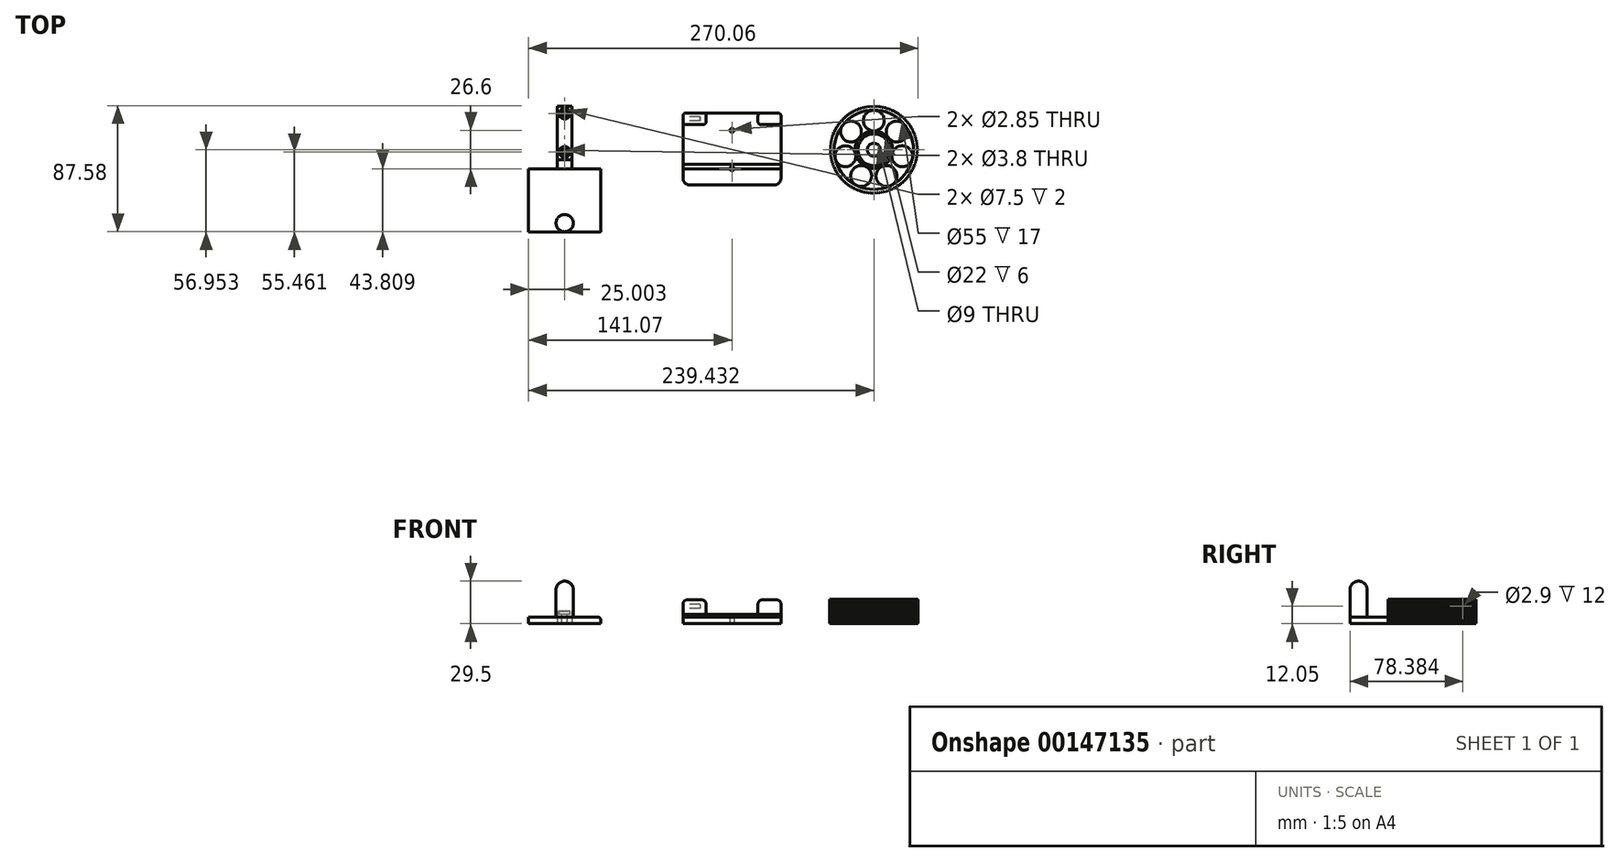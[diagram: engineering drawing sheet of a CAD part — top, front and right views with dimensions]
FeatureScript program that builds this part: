
annotation { "Feature Type Name" : "Feature", "Feature Type Description" : "" }
export const myFeature = defineFeature(function(context is Context, id is Id, definition is map)
    precondition{}
    {
        {
            var Q0;
            Q0=qCreatedBy(makeId("Top.planeOp"),FACE);
            var sketch = newSketch(context, id + "F0", { "sketchPlane" : qUnion([Q0])});
            skLineSegment(sketch, "E0.bottom", {"start": v(-34, 21.3) * mm, "end": v(34, 21.3) * mm});
            skLineSegment(sketch, "E0.top", {"start": v(-34, -28.7) * mm, "end": v(34, -28.7) * mm});
            skLineSegment(sketch, "E0.left", {"start": v(-34, 21.3) * mm, "end": v(-34, -28.7) * mm});
            skLineSegment(sketch, "E0.right", {"start": v(34, 21.3) * mm, "end": v(34, -28.7) * mm});
            skCircle(sketch, "E1", {"center": v(0, 9.32) * mm, "radius": 1.43 * mm});
            skCircle(sketch, "E2", {"center": v(0, -17.28) * mm, "radius": 1.43 * mm});
            skSolve(sketch);
        }
        {
            var Q0;
            Q0=makeQuery(id+"F0.imprint","IMPRINT",FACE,{"disambiguationData":[TD([[makeQuery(id+"F0.imprint","IMPRINT",EDGE,{"derivedFrom":sQuery(id+"F0.wireOp",EDGE,"E0.bottom")}),-1.0]])]});
            extrude(context, id + "F1", {"entities" : qUnion([Q0]), "depth" : 6.5 * mm});
        }
        {
            var Q0;
            Q0=makeQuery(id+"F1.opExtrude","CAP_FACE",FACE,{"disambiguationData":[OSD([sQuery(id+"F0.wireOp",EDGE,"E0.bottom"),sQuery(id+"F0.wireOp",EDGE,"E0.top"),sQuery(id+"F0.wireOp",EDGE,"E0.left"),sQuery(id+"F0.wireOp",EDGE,"E0.right"),sQuery(id+"F0.wireOp",EDGE,"E1"),sQuery(id+"F0.wireOp",EDGE,"E2")])],"isStart":false});
            var sketch = newSketch(context, id + "F2", { "sketchPlane" : qUnion([Q0])});
            skLineSegment(sketch, "E3.bottom", {"start": v(-34, 21.3) * mm, "end": v(-18, 21.3) * mm});
            skLineSegment(sketch, "E3.top", {"start": v(-34, 13.3) * mm, "end": v(-18, 13.3) * mm});
            skLineSegment(sketch, "E3.left", {"start": v(-34, 21.3) * mm, "end": v(-34, 13.3) * mm});
            skLineSegment(sketch, "E3.right", {"start": v(-18, 21.3) * mm, "end": v(-18, 13.3) * mm});
            skLineSegment(sketch, "E4.bottom", {"start": v(34, 21.3) * mm, "end": v(18, 21.3) * mm});
            skLineSegment(sketch, "E4.top", {"start": v(34, 13.3) * mm, "end": v(18, 13.3) * mm});
            skLineSegment(sketch, "E4.left", {"start": v(34, 21.3) * mm, "end": v(34, 13.3) * mm});
            skLineSegment(sketch, "E4.right", {"start": v(18, 21.3) * mm, "end": v(18, 13.3) * mm});
            skSolve(sketch);
        }
        {
            var Q0;
            Q0=makeQuery(id+"F2.imprint","IMPRINT",FACE,{"disambiguationData":[TD([[makeQuery(id+"F2.imprint","IMPRINT",EDGE,{"derivedFrom":sQuery(id+"F2.wireOp",EDGE,"E3.bottom")}),-1.0]])]});
            var Q1;
            Q1=makeQuery(id+"F2.imprint","IMPRINT",FACE,{"disambiguationData":[TD([[makeQuery(id+"F2.imprint","IMPRINT",EDGE,{"derivedFrom":sQuery(id+"F2.wireOp",EDGE,"E4.bottom")}),-1.0]])]});
            extrude(context, id + "F3", {"entities" : qUnion([Q0, Q1]), "operationType" : NewBodyOperationType.ADD, "depth" : 10 * mm});
        }
        {
            var Q0;
            Q0=makeQuery(id+"F3.boolean.opBoolean","MERGE",FACE,{"derivedFrom":[makeQuery(id+"F1.opExtrude","SWEPT_FACE",FACE,{"disambiguationData":[OSD([sQuery(id+"F0.wireOp",EDGE,"E0.left")])]}),makeQuery(id+"F3.opExtrude","SWEPT_FACE",FACE,{"disambiguationData":[OSD([sQuery(id+"F2.wireOp",EDGE,"E3.left")])]})]});
            var sketch = newSketch(context, id + "F4", { "sketchPlane" : qUnion([Q0])});
            skCircle(sketch, "E5", {"center": v(-17.3, 12.05) * mm, "radius": 1.45 * mm});
            skSolve(sketch);
        }
        {
            var Q0;
            Q0=makeQuery(id+"F4.imprint","IMPRINT",FACE,{"disambiguationData":[TD([[makeQuery(id+"F4.imprint","IMPRINT",EDGE,{"derivedFrom":sQuery(id+"F4.wireOp",EDGE,"E5")}),1.0]])]});
            extrude(context, id + "F5", {"entities" : qUnion([Q0]), "operationType" : NewBodyOperationType.REMOVE, "oppositeDirection" : true, "depth" : 12 * mm});
        }
        {
            var Q0;
            Q0=makeQuery(id+"F1.opExtrude","SWEPT_EDGE",EDGE,{"disambiguationData":[OSD([sQuery(id+"F0.wireOp",EDGE,"E0.top"),sQuery(id+"F0.wireOp",EDGE,"E0.left")])]});
            var Q1;
            Q1=makeQuery(id+"F1.opExtrude","SWEPT_EDGE",EDGE,{"disambiguationData":[OSD([sQuery(id+"F0.wireOp",EDGE,"E0.top"),sQuery(id+"F0.wireOp",EDGE,"E0.right")])]});
            fillet(context, id + "F6", {"entities" : qUnion([Q0, Q1]), "radius" : 5 * mm, "tangentPropagation" : true, "allowEdgeOverflow" : false});
        }
        {
            var Q0;
            Q0=makeQuery(id+"F3.opExtrude","CAP_EDGE",EDGE,{"disambiguationData":[OSD([sQuery(id+"F2.wireOp",EDGE,"E3.left")])],"isStart":false});
            var Q1;
            Q1=makeQuery(id+"F3.opExtrude","CAP_EDGE",EDGE,{"disambiguationData":[OSD([sQuery(id+"F2.wireOp",EDGE,"E4.left")])],"isStart":false});
            var Q2;
            Q2=makeQuery(id+"F3.opExtrude","CAP_EDGE",EDGE,{"disambiguationData":[OSD([sQuery(id+"F2.wireOp",EDGE,"E3.right")])],"isStart":false});
            var Q3;
            Q3=makeQuery(id+"F3.opExtrude","CAP_EDGE",EDGE,{"disambiguationData":[OSD([sQuery(id+"F2.wireOp",EDGE,"E4.right")])],"isStart":false});
            fillet(context, id + "F7", {"entities" : qUnion([Q0, Q1, Q2, Q3]), "radius" : 3 * mm, "tangentPropagation" : true, "allowEdgeOverflow" : false});
        }
        {
            var Q0;
            Q0=qCreatedBy(makeId("Top.planeOp"),FACE);
            var sketch = newSketch(context, id + "F8", { "sketchPlane" : qUnion([Q0])});
            skLineSegment(sketch, "E6.bottom", {"start": v(-121.07, 25.97) * mm, "end": v(-111.07, 25.97) * mm});
            skLineSegment(sketch, "E6.left", {"start": v(-121.07, 25.97) * mm, "end": v(-121.07, -17.53) * mm});
            skLineSegment(sketch, "E6.right", {"start": v(-111.07, 25.97) * mm, "end": v(-111.07, -17.53) * mm});
            skLineSegment(sketch, "E7.bottom", {"start": v(-141.07, -17.53) * mm, "end": v(-121.07, -17.53) * mm});
            skLineSegment(sketch, "E7.top", {"start": v(-141.07, -61.1) * mm, "end": v(-91.07, -61.1) * mm});
            skLineSegment(sketch, "E7.left", {"start": v(-141.07, -17.53) * mm, "end": v(-141.07, -61.1) * mm});
            skLineSegment(sketch, "E7.right", {"start": v(-91.07, -17.53) * mm, "end": v(-91.07, -61.1) * mm});
            skLineSegment(sketch, "E8.trimOffspring", {"start": v(-111.07, -17.53) * mm, "end": v(-91.07, -17.53) * mm});
            skSolve(sketch);
        }
        {
            var Q0;
            Q0=makeQuery(id+"F8.imprint","IMPRINT",FACE,{"disambiguationData":[TD([[makeQuery(id+"F8.imprint","IMPRINT",EDGE,{"derivedFrom":sQuery(id+"F8.wireOp",EDGE,"E6.bottom")}),-1.0]])]});
            extrude(context, id + "F9", {"entities" : qUnion([Q0]), "depth" : 8.5 * mm});
        }
        {
            var Q0;
            Q0=makeQuery(id+"F9.opExtrude","SWEPT_FACE",FACE,{"disambiguationData":[OSD([sQuery(id+"F8.wireOp",EDGE,"E7.left")])]});
            var sketch = newSketch(context, id + "F10", { "sketchPlane" : qUnion([Q0])});
            skLineSegment(sketch, "E9", {"start": v(61.1, 4.5) * mm, "end": v(17.53, 4.5) * mm});
            skLineSegment(sketch, "E10", {"start": v(17.53, 4.5) * mm, "end": v(11.03, 8.5) * mm});
            skLineSegment(sketch, "E11", {"start": v(11.03, 8.5) * mm, "end": v(61.1, 8.5) * mm});
            skLineSegment(sketch, "E12", {"start": v(61.1, 8.5) * mm, "end": v(61.1, 4.5) * mm});
            skSolve(sketch);
        }
        {
            var Q0;
            {var subQ0=sQuery(id+"F10.wireOp",EDGE,"E10");Q0=makeQuery(id+"F10.imprint","IMPRINT",FACE,{"disambiguationData":[TD([[makeQuery(id+"F10.imprint","IMPRINT",EDGE,{"derivedFrom":subQ0}),-1.0]])]});}
            var Q1;
            {var subQ0=sQuery(id+"F10.wireOp",EDGE,"E9");Q1=makeQuery(id+"F10.imprint","IMPRINT",FACE,{"disambiguationData":[TD([[makeQuery(id+"F10.imprint","IMPRINT",EDGE,{"derivedFrom":subQ0}),-1.0]])]});}
            extrude(context, id + "F11", {"entities" : qUnion([Q0, Q1]), "operationType" : NewBodyOperationType.REMOVE, "endBound" : BoundingType.THROUGH_ALL, "oppositeDirection" : true, "depth" : 25 * mm});
        }
        {
            var Q0;
            Q0=makeQuery(id+"F9.opExtrude","CAP_FACE",FACE,{"disambiguationData":[OSD([sQuery(id+"F8.wireOp",EDGE,"E6.bottom"),sQuery(id+"F8.wireOp",EDGE,"E6.left"),sQuery(id+"F8.wireOp",EDGE,"E6.right"),sQuery(id+"F8.wireOp",EDGE,"E7.bottom"),sQuery(id+"F8.wireOp",EDGE,"E7.top"),sQuery(id+"F8.wireOp",EDGE,"E7.left"),sQuery(id+"F8.wireOp",EDGE,"E7.right"),sQuery(id+"F8.wireOp",EDGE,"E8.trimOffspring")])],"isStart":false});
            var sketch = newSketch(context, id + "F12", { "sketchPlane" : qUnion([Q0])});
            skLineSegment(sketch, "E13", {"start": v(-116.07, 25.97) * mm, "end": v(-116.07, -11.03) * mm, "construction": true});
            skCircle(sketch, "E14", {"center": v(-116.07, 20.97) * mm, "radius": 3.75 * mm});
            skCircle(sketch, "E15", {"center": v(-116.07, -5.63) * mm, "radius": 3.75 * mm});
            skCircle(sketch, "E16", {"center": v(-116.07, 20.97) * mm, "radius": 1.9 * mm});
            skCircle(sketch, "E17", {"center": v(-116.07, -5.63) * mm, "radius": 1.9 * mm});
            skSolve(sketch);
        }
        {
            var Q0;
            Q0=makeQuery(id+"F12.imprint","IMPRINT",FACE,{"disambiguationData":[TD([[makeQuery(id+"F12.imprint","IMPRINT",EDGE,{"derivedFrom":sQuery(id+"F12.wireOp",EDGE,"E16")}),1.0]])]});
            var Q1;
            Q1=makeQuery(id+"F12.imprint","IMPRINT",FACE,{"disambiguationData":[TD([[makeQuery(id+"F12.imprint","IMPRINT",EDGE,{"derivedFrom":sQuery(id+"F12.wireOp",EDGE,"E17")}),1.0]])]});
            extrude(context, id + "F13", {"entities" : qUnion([Q0, Q1]), "operationType" : NewBodyOperationType.REMOVE, "endBound" : BoundingType.THROUGH_ALL, "oppositeDirection" : true, "depth" : 25 * mm});
        }
        {
            var Q0;
            Q0=makeQuery(id+"F12.imprint","IMPRINT",FACE,{"disambiguationData":[TD([[makeQuery(id+"F12.imprint","IMPRINT",EDGE,{"derivedFrom":sQuery(id+"F12.wireOp",EDGE,"E14")}),1.0]])]});
            var Q1;
            Q1=makeQuery(id+"F12.imprint","IMPRINT",FACE,{"disambiguationData":[TD([[makeQuery(id+"F12.imprint","IMPRINT",EDGE,{"derivedFrom":sQuery(id+"F12.wireOp",EDGE,"E15")}),1.0]])]});
            extrude(context, id + "F14", {"entities" : qUnion([Q0, Q1]), "operationType" : NewBodyOperationType.REMOVE, "oppositeDirection" : true, "depth" : 2 * mm});
        }
        {
            var Q0;
            Q0=makeQuery(id+"F11.boolean.opBoolean","COPY",FACE,{"derivedFrom":makeQuery(id+"F11.opExtrude","SWEPT_FACE",FACE,{"disambiguationData":[OSD([sQuery(id+"F10.wireOp",EDGE,"E9")])]})});
            var sketch = newSketch(context, id + "F15", { "sketchPlane" : qUnion([Q0])});
            skCircle(sketch, "E18", {"center": v(-116.07, -55.1) * mm, "radius": 6 * mm});
            skSolve(sketch);
        }
        {
            var Q0;
            Q0=makeQuery(id+"F15.imprint","IMPRINT",FACE,{"disambiguationData":[TD([[makeQuery(id+"F15.imprint","IMPRINT",EDGE,{"derivedFrom":sQuery(id+"F15.wireOp",EDGE,"E18")}),1.0]])]});
            extrude(context, id + "F16", {"entities" : qUnion([Q0]), "operationType" : NewBodyOperationType.ADD, "depth" : 25 * mm});
        }
        {
            var Q0;
            Q0=makeQuery(id+"F16.opExtrude","CAP_EDGE",EDGE,{"disambiguationData":[OSD([sQuery(id+"F15.wireOp",EDGE,"E18")])],"isStart":false});
            fillet(context, id + "F17", {"entities" : qUnion([Q0]), "radius" : 6 * mm, "tangentPropagation" : true, "allowEdgeOverflow" : false});
        }
        {
            var Q0;
            Q0=makeQuery(id+"F11.boolean.opBoolean","COPY",EDGE,{"derivedFrom":makeQuery(id+"F11.opExtrude","CAP_EDGE",EDGE,{"disambiguationData":[OSD([sQuery(id+"F10.wireOp",EDGE,"E9")])],"isStart":true})});
            var Q1;
            {var subQ0=sQuery(id+"F8.wireOp",EDGE,"E7.top");var subQ1=sQuery(id+"F8.wireOp",EDGE,"E7.left");var subQ2=sQuery(id+"F10.wireOp",EDGE,"E9");Q1=makeQuery(id+"F16.boolean.opBoolean","SPLIT",EDGE,{"disambiguationData":[TD([makeQuery(id+"F9.opExtrude","SWEPT_FACE",FACE,{"disambiguationData":[OSD([subQ1])]})])],"derivedFrom":makeQuery(id+"F11.boolean.opBoolean","COPY",EDGE,{"derivedFrom":makeQuery(id+"F11.opExtrude","SWEPT_EDGE",EDGE,{"disambiguationData":[OSD([subQ0,subQ1,subQ2,sQuery(id+"F10.wireOp",EDGE,"E12")])]})})});}
            var Q2;
            {var subQ0=sQuery(id+"F8.wireOp",EDGE,"E7.top");var subQ1=sQuery(id+"F10.wireOp",EDGE,"E9");Q2=makeQuery(id+"F16.boolean.opBoolean","SPLIT",EDGE,{"disambiguationData":[TD([makeQuery(id+"F9.opExtrude","SWEPT_FACE",FACE,{"disambiguationData":[OSD([sQuery(id+"F8.wireOp",EDGE,"E7.right")])]})])],"derivedFrom":makeQuery(id+"F11.boolean.opBoolean","COPY",EDGE,{"derivedFrom":makeQuery(id+"F11.opExtrude","SWEPT_EDGE",EDGE,{"disambiguationData":[OSD([subQ0,sQuery(id+"F8.wireOp",EDGE,"E7.left"),subQ1,sQuery(id+"F10.wireOp",EDGE,"E12")])]})})});}
            var Q3;
            Q3=makeQuery(id+"F11.boolean.opBoolean","INTERSECT",EDGE,{"derivedFrom":[makeQuery(id+"F9.opExtrude","SWEPT_FACE",FACE,{"disambiguationData":[OSD([sQuery(id+"F8.wireOp",EDGE,"E7.right")])]}),makeQuery(id+"F11.opExtrude","SWEPT_FACE",FACE,{"disambiguationData":[OSD([sQuery(id+"F10.wireOp",EDGE,"E9")])]})]});
            fillet(context, id + "F18", {"entities" : qUnion([Q0, Q1, Q2, Q3]), "radius" : 2 * mm, "tangentPropagation" : true, "allowEdgeOverflow" : false});
        }
        {
            var Q0;
            Q0=qCreatedBy(makeId("Top.planeOp"),FACE);
            var sketch = newSketch(context, id + "F19", { "sketchPlane" : qUnion([Q0])});
            skArc(sketch, "E19", {"start": v(98.36, 25.86) * mm, "mid": v(98.14, 25.86) * mm, "end": v(97.92, 25.86) * mm});
            skCircle(sketch, "E20", {"center": v(98.36, -4.14) * mm, "radius": 27.5 * mm});
            skCircle(sketch, "E21", {"center": v(98.36, -4.14) * mm, "radius": 11 * mm});
            skCircle(sketch, "E22", {"center": v(98.36, -4.14) * mm, "radius": 13 * mm});
            skCircle(sketch, "E23", {"center": v(98.36, -4.14) * mm, "radius": 4.5 * mm});
            skLineSegment(sketch, "E24", {"start": v(98.36, -4.14) * mm, "end": v(98.36, 23.36) * mm, "construction": true});
            skCircle(sketch, "E25", {"center": v(98.36, 16.11) * mm, "radius": 7.25 * mm});
            skCircle(sketch, "E26.1.0", {"center": v(82.53, 8.49) * mm, "radius": 7.25 * mm});
            skLineSegment(sketch, "E26.1.1", {"start": v(98.36, -4.14) * mm, "end": v(76.86, 13) * mm, "construction": true});
            skCircle(sketch, "E26.2.0", {"center": v(78.62, -8.64) * mm, "radius": 7.25 * mm});
            skLineSegment(sketch, "E26.2.1", {"start": v(98.36, -4.14) * mm, "end": v(71.55, -10.26) * mm, "construction": true});
            skCircle(sketch, "E26.3.0", {"center": v(89.58, -22.38) * mm, "radius": 7.25 * mm});
            skLineSegment(sketch, "E26.3.1", {"start": v(98.36, -4.14) * mm, "end": v(86.43, -28.91) * mm, "construction": true});
            skCircle(sketch, "E26.4.0", {"center": v(107.15, -22.38) * mm, "radius": 7.25 * mm});
            skLineSegment(sketch, "E26.4.1", {"start": v(98.36, -4.14) * mm, "end": v(110.3, -28.91) * mm, "construction": true});
            skCircle(sketch, "E26.5.0", {"center": v(118.1, -8.64) * mm, "radius": 7.25 * mm});
            skLineSegment(sketch, "E26.5.1", {"start": v(98.36, -4.14) * mm, "end": v(125.17, -10.26) * mm, "construction": true});
            skLineSegment(sketch, "E27", {"start": v(98.36, 23.36) * mm, "end": v(98.36, 25.86) * mm, "construction": true});
            skLineSegment(sketch, "E28", {"start": v(98.36, 25.86) * mm, "end": v(98.82, 26.5) * mm});
            skLineSegment(sketch, "E29", {"start": v(98.82, 26.5) * mm, "end": v(99.17, 25.85) * mm});
            skLineSegment(sketch, "E30.1.0", {"start": v(97.1, 25.84) * mm, "end": v(97.53, 26.48) * mm});
            skLineSegment(sketch, "E30.1.1", {"start": v(97.53, 26.48) * mm, "end": v(97.92, 25.86) * mm});
            skLineSegment(sketch, "E30.2.0", {"start": v(95.85, 25.76) * mm, "end": v(96.25, 26.42) * mm});
            skLineSegment(sketch, "E30.2.1", {"start": v(96.25, 26.42) * mm, "end": v(96.66, 25.81) * mm});
            skLineSegment(sketch, "E30.3.0", {"start": v(94.6, 25.63) * mm, "end": v(94.97, 26.3) * mm});
            skLineSegment(sketch, "E30.3.1", {"start": v(94.97, 26.3) * mm, "end": v(95.4, 25.72) * mm});
            skLineSegment(sketch, "E30.4.0", {"start": v(93.36, 25.44) * mm, "end": v(93.7, 26.14) * mm});
            skLineSegment(sketch, "E30.4.1", {"start": v(93.7, 26.14) * mm, "end": v(94.16, 25.57) * mm});
            skLineSegment(sketch, "E30.5.0", {"start": v(92.12, 25.2) * mm, "end": v(92.44, 25.92) * mm});
            skLineSegment(sketch, "E30.5.1", {"start": v(92.44, 25.92) * mm, "end": v(92.92, 25.36) * mm});
            skLineSegment(sketch, "E30.6.0", {"start": v(90.9, 24.92) * mm, "end": v(91.19, 25.64) * mm});
            skLineSegment(sketch, "E30.6.1", {"start": v(91.19, 25.64) * mm, "end": v(91.69, 25.11) * mm});
            skLineSegment(sketch, "E30.7.0", {"start": v(89.7, 24.58) * mm, "end": v(89.95, 25.32) * mm});
            skLineSegment(sketch, "E30.7.1", {"start": v(89.95, 25.32) * mm, "end": v(90.47, 24.8) * mm});
            skLineSegment(sketch, "E30.8.0", {"start": v(88.5, 24.2) * mm, "end": v(88.72, 24.94) * mm});
            skLineSegment(sketch, "E30.8.1", {"start": v(88.72, 24.94) * mm, "end": v(89.27, 24.45) * mm});
            skLineSegment(sketch, "E30.9.0", {"start": v(87.32, 23.76) * mm, "end": v(87.5, 24.5) * mm});
            skLineSegment(sketch, "E30.9.1", {"start": v(87.5, 24.5) * mm, "end": v(88.08, 24.04) * mm});
            skLineSegment(sketch, "E30.10.0", {"start": v(86.16, 23.27) * mm, "end": v(86.32, 24.03) * mm});
            skLineSegment(sketch, "E30.10.1", {"start": v(86.32, 24.03) * mm, "end": v(86.9, 23.59) * mm});
            skLineSegment(sketch, "E30.11.0", {"start": v(85.02, 22.73) * mm, "end": v(85.15, 23.5) * mm});
            skLineSegment(sketch, "E30.11.1", {"start": v(85.15, 23.5) * mm, "end": v(85.75, 23.08) * mm});
            skLineSegment(sketch, "E30.12.0", {"start": v(83.9, 22.15) * mm, "end": v(84, 22.92) * mm});
            skLineSegment(sketch, "E30.12.1", {"start": v(84, 22.92) * mm, "end": v(84.63, 22.53) * mm});
            skLineSegment(sketch, "E30.13.0", {"start": v(82.82, 21.52) * mm, "end": v(82.88, 22.3) * mm});
            skLineSegment(sketch, "E30.13.1", {"start": v(82.88, 22.3) * mm, "end": v(83.52, 21.93) * mm});
            skLineSegment(sketch, "E30.14.0", {"start": v(81.76, 20.85) * mm, "end": v(81.8, 21.63) * mm});
            skLineSegment(sketch, "E30.14.1", {"start": v(81.8, 21.63) * mm, "end": v(82.44, 21.29) * mm});
            skLineSegment(sketch, "E30.15.0", {"start": v(80.73, 20.13) * mm, "end": v(80.73, 20.9) * mm});
            skLineSegment(sketch, "E30.15.1", {"start": v(80.73, 20.9) * mm, "end": v(81.4, 20.6) * mm});
            skLineSegment(sketch, "E30.16.0", {"start": v(79.73, 19.37) * mm, "end": v(79.7, 20.15) * mm});
            skLineSegment(sketch, "E30.16.1", {"start": v(79.7, 20.15) * mm, "end": v(80.37, 19.87) * mm});
            skLineSegment(sketch, "E30.17.0", {"start": v(78.76, 18.57) * mm, "end": v(78.7, 19.35) * mm});
            skLineSegment(sketch, "E30.17.1", {"start": v(78.7, 19.35) * mm, "end": v(79.38, 19.1) * mm});
            skLineSegment(sketch, "E30.18.0", {"start": v(77.83, 17.73) * mm, "end": v(77.73, 18.5) * mm});
            skLineSegment(sketch, "E30.18.1", {"start": v(77.73, 18.5) * mm, "end": v(78.42, 18.28) * mm});
            skLineSegment(sketch, "E30.19.0", {"start": v(76.93, 16.85) * mm, "end": v(76.8, 17.62) * mm});
            skLineSegment(sketch, "E30.19.1", {"start": v(76.8, 17.62) * mm, "end": v(77.5, 17.42) * mm});
            skLineSegment(sketch, "E30.20.0", {"start": v(76.07, 15.94) * mm, "end": v(75.9, 16.7) * mm});
            skLineSegment(sketch, "E30.20.1", {"start": v(75.9, 16.7) * mm, "end": v(76.62, 16.53) * mm});
            skLineSegment(sketch, "E30.21.0", {"start": v(75.25, 14.99) * mm, "end": v(75.05, 15.74) * mm});
            skLineSegment(sketch, "E30.21.1", {"start": v(75.05, 15.74) * mm, "end": v(75.77, 15.6) * mm});
            skLineSegment(sketch, "E30.22.0", {"start": v(74.47, 14) * mm, "end": v(74.24, 14.74) * mm});
            skLineSegment(sketch, "E30.22.1", {"start": v(74.24, 14.74) * mm, "end": v(74.97, 14.64) * mm});
            skLineSegment(sketch, "E30.23.0", {"start": v(73.73, 12.98) * mm, "end": v(73.47, 13.72) * mm});
            skLineSegment(sketch, "E30.23.1", {"start": v(73.47, 13.72) * mm, "end": v(74.2, 13.64) * mm});
            skLineSegment(sketch, "E30.24.0", {"start": v(73.03, 11.94) * mm, "end": v(72.75, 12.66) * mm});
            skLineSegment(sketch, "E30.24.1", {"start": v(72.75, 12.66) * mm, "end": v(73.48, 12.62) * mm});
            skLineSegment(sketch, "E30.25.0", {"start": v(72.38, 10.86) * mm, "end": v(72.06, 11.57) * mm});
            skLineSegment(sketch, "E30.25.1", {"start": v(72.06, 11.57) * mm, "end": v(72.8, 11.56) * mm});
            skLineSegment(sketch, "E30.26.0", {"start": v(71.78, 9.76) * mm, "end": v(71.43, 10.46) * mm});
            skLineSegment(sketch, "E30.26.1", {"start": v(71.43, 10.46) * mm, "end": v(72.16, 10.47) * mm});
            skLineSegment(sketch, "E30.27.0", {"start": v(71.22, 8.64) * mm, "end": v(70.84, 9.32) * mm});
            skLineSegment(sketch, "E30.27.1", {"start": v(70.84, 9.32) * mm, "end": v(71.57, 9.36) * mm});
            skLineSegment(sketch, "E30.28.0", {"start": v(70.7, 7.49) * mm, "end": v(70.3, 8.15) * mm});
            skLineSegment(sketch, "E30.28.1", {"start": v(70.3, 8.15) * mm, "end": v(71.03, 8.23) * mm});
            skLineSegment(sketch, "E30.29.0", {"start": v(70.24, 6.32) * mm, "end": v(69.81, 6.97) * mm});
            skLineSegment(sketch, "E30.29.1", {"start": v(69.81, 6.97) * mm, "end": v(70.54, 7.08) * mm});
            skLineSegment(sketch, "E30.30.0", {"start": v(69.83, 5.13) * mm, "end": v(69.37, 5.76) * mm});
            skLineSegment(sketch, "E30.30.1", {"start": v(69.37, 5.76) * mm, "end": v(70.1, 5.9) * mm});
            skLineSegment(sketch, "E30.31.0", {"start": v(69.47, 3.93) * mm, "end": v(68.98, 4.54) * mm});
            skLineSegment(sketch, "E30.31.1", {"start": v(68.98, 4.54) * mm, "end": v(69.7, 4.7) * mm});
            skLineSegment(sketch, "E30.32.0", {"start": v(69.15, 2.71) * mm, "end": v(68.65, 3.3) * mm});
            skLineSegment(sketch, "E30.32.1", {"start": v(68.65, 3.3) * mm, "end": v(69.35, 3.5) * mm});
            skLineSegment(sketch, "E30.33.0", {"start": v(68.9, 1.48) * mm, "end": v(68.36, 2.05) * mm});
            skLineSegment(sketch, "E30.33.1", {"start": v(68.36, 2.05) * mm, "end": v(69.06, 2.28) * mm});
            skLineSegment(sketch, "E30.34.0", {"start": v(68.68, 0.25) * mm, "end": v(68.13, 0.79) * mm});
            skLineSegment(sketch, "E30.34.1", {"start": v(68.13, 0.79) * mm, "end": v(68.81, 1.05) * mm});
            skLineSegment(sketch, "E30.35.0", {"start": v(68.53, -1) * mm, "end": v(67.95, -0.48) * mm});
            skLineSegment(sketch, "E30.35.1", {"start": v(67.95, -0.48) * mm, "end": v(68.62, -0.2) * mm});
            skLineSegment(sketch, "E30.36.0", {"start": v(68.42, -2.25) * mm, "end": v(67.82, -1.76) * mm});
            skLineSegment(sketch, "E30.36.1", {"start": v(67.82, -1.76) * mm, "end": v(68.48, -1.45) * mm});
            skLineSegment(sketch, "E30.37.0", {"start": v(68.37, -3.5) * mm, "end": v(67.75, -3.04) * mm});
            skLineSegment(sketch, "E30.37.1", {"start": v(67.75, -3.04) * mm, "end": v(68.4, -2.7) * mm});
            skLineSegment(sketch, "E30.38.0", {"start": v(68.37, -4.77) * mm, "end": v(67.73, -4.32) * mm});
            skLineSegment(sketch, "E30.38.1", {"start": v(67.73, -4.32) * mm, "end": v(68.36, -3.96) * mm});
            skLineSegment(sketch, "E30.39.0", {"start": v(68.42, -6.02) * mm, "end": v(67.77, -5.6) * mm});
            skLineSegment(sketch, "E30.39.1", {"start": v(67.77, -5.6) * mm, "end": v(68.38, -5.21) * mm});
            skLineSegment(sketch, "E30.40.0", {"start": v(68.53, -7.27) * mm, "end": v(67.85, -6.89) * mm});
            skLineSegment(sketch, "E30.40.1", {"start": v(67.85, -6.89) * mm, "end": v(68.45, -6.47) * mm});
            skLineSegment(sketch, "E30.41.0", {"start": v(68.68, -8.52) * mm, "end": v(68, -8.16) * mm});
            skLineSegment(sketch, "E30.41.1", {"start": v(68, -8.16) * mm, "end": v(68.58, -7.72) * mm});
            skLineSegment(sketch, "E30.42.0", {"start": v(68.9, -9.76) * mm, "end": v(68.2, -9.43) * mm});
            skLineSegment(sketch, "E30.42.1", {"start": v(68.2, -9.43) * mm, "end": v(68.75, -8.96) * mm});
            skLineSegment(sketch, "E30.43.0", {"start": v(69.15, -10.99) * mm, "end": v(68.44, -10.69) * mm});
            skLineSegment(sketch, "E30.43.1", {"start": v(68.44, -10.69) * mm, "end": v(68.98, -10.2) * mm});
            skLineSegment(sketch, "E30.44.0", {"start": v(69.47, -12.2) * mm, "end": v(68.74, -11.94) * mm});
            skLineSegment(sketch, "E30.44.1", {"start": v(68.74, -11.94) * mm, "end": v(69.26, -11.42) * mm});
            skLineSegment(sketch, "E30.45.0", {"start": v(69.83, -13.4) * mm, "end": v(69.1, -13.17) * mm});
            skLineSegment(sketch, "E30.45.1", {"start": v(69.1, -13.17) * mm, "end": v(69.6, -12.63) * mm});
            skLineSegment(sketch, "E30.46.0", {"start": v(70.24, -14.6) * mm, "end": v(69.5, -14.39) * mm});
            skLineSegment(sketch, "E30.46.1", {"start": v(69.5, -14.39) * mm, "end": v(69.97, -13.83) * mm});
            skLineSegment(sketch, "E30.47.0", {"start": v(70.7, -15.76) * mm, "end": v(69.95, -15.59) * mm});
            skLineSegment(sketch, "E30.47.1", {"start": v(69.95, -15.59) * mm, "end": v(70.4, -15.01) * mm});
            skLineSegment(sketch, "E30.48.0", {"start": v(71.22, -16.91) * mm, "end": v(70.45, -16.77) * mm});
            skLineSegment(sketch, "E30.48.1", {"start": v(70.45, -16.77) * mm, "end": v(70.88, -16.17) * mm});
            skLineSegment(sketch, "E30.49.0", {"start": v(71.78, -18.04) * mm, "end": v(71, -17.92) * mm});
            skLineSegment(sketch, "E30.49.1", {"start": v(71, -17.92) * mm, "end": v(71.41, -17.31) * mm});
            skLineSegment(sketch, "E30.50.0", {"start": v(72.38, -19.14) * mm, "end": v(71.6, -19.06) * mm});
            skLineSegment(sketch, "E30.50.1", {"start": v(71.6, -19.06) * mm, "end": v(71.99, -18.43) * mm});
            skLineSegment(sketch, "E30.51.0", {"start": v(73.03, -20.21) * mm, "end": v(72.26, -20.17) * mm});
            skLineSegment(sketch, "E30.51.1", {"start": v(72.26, -20.17) * mm, "end": v(72.6, -19.52) * mm});
            skLineSegment(sketch, "E30.52.0", {"start": v(73.73, -21.26) * mm, "end": v(72.95, -21.24) * mm});
            skLineSegment(sketch, "E30.52.1", {"start": v(72.95, -21.24) * mm, "end": v(73.27, -20.59) * mm});
            skLineSegment(sketch, "E30.53.0", {"start": v(74.47, -22.28) * mm, "end": v(73.7, -22.3) * mm});
            skLineSegment(sketch, "E30.53.1", {"start": v(73.7, -22.3) * mm, "end": v(73.99, -21.62) * mm});
            skLineSegment(sketch, "E30.54.0", {"start": v(75.25, -23.26) * mm, "end": v(74.47, -23.31) * mm});
            skLineSegment(sketch, "E30.54.1", {"start": v(74.47, -23.31) * mm, "end": v(74.74, -22.63) * mm});
            skLineSegment(sketch, "E30.55.0", {"start": v(76.07, -24.21) * mm, "end": v(75.3, -24.3) * mm});
            skLineSegment(sketch, "E30.55.1", {"start": v(75.3, -24.3) * mm, "end": v(75.53, -23.6) * mm});
            skLineSegment(sketch, "E30.56.0", {"start": v(76.93, -25.13) * mm, "end": v(76.16, -25.24) * mm});
            skLineSegment(sketch, "E30.56.1", {"start": v(76.16, -25.24) * mm, "end": v(76.37, -24.54) * mm});
            skLineSegment(sketch, "E30.57.0", {"start": v(77.83, -26) * mm, "end": v(77.06, -26.15) * mm});
            skLineSegment(sketch, "E30.57.1", {"start": v(77.06, -26.15) * mm, "end": v(77.24, -25.44) * mm});
            skLineSegment(sketch, "E30.58.0", {"start": v(78.76, -26.85) * mm, "end": v(78, -27.03) * mm});
            skLineSegment(sketch, "E30.58.1", {"start": v(78, -27.03) * mm, "end": v(78.15, -26.3) * mm});
            skLineSegment(sketch, "E30.59.0", {"start": v(79.73, -27.65) * mm, "end": v(78.98, -27.86) * mm});
            skLineSegment(sketch, "E30.59.1", {"start": v(78.98, -27.86) * mm, "end": v(79.1, -27.14) * mm});
            skLineSegment(sketch, "E30.60.0", {"start": v(80.73, -28.4) * mm, "end": v(80, -28.65) * mm});
            skLineSegment(sketch, "E30.60.1", {"start": v(80, -28.65) * mm, "end": v(80.08, -27.92) * mm});
            skLineSegment(sketch, "E30.61.0", {"start": v(81.76, -29.12) * mm, "end": v(81.03, -29.4) * mm});
            skLineSegment(sketch, "E30.61.1", {"start": v(81.03, -29.4) * mm, "end": v(81.1, -28.67) * mm});
            skLineSegment(sketch, "E30.62.0", {"start": v(82.82, -29.8) * mm, "end": v(82.1, -30.1) * mm});
            skLineSegment(sketch, "E30.62.1", {"start": v(82.1, -30.1) * mm, "end": v(82.13, -29.37) * mm});
            skLineSegment(sketch, "E30.63.0", {"start": v(83.9, -30.43) * mm, "end": v(83.2, -30.76) * mm});
            skLineSegment(sketch, "E30.63.1", {"start": v(83.2, -30.76) * mm, "end": v(83.2, -30.03) * mm});
            skLineSegment(sketch, "E30.64.0", {"start": v(85.02, -31) * mm, "end": v(84.34, -31.37) * mm});
            skLineSegment(sketch, "E30.64.1", {"start": v(84.34, -31.37) * mm, "end": v(84.3, -30.64) * mm});
            skLineSegment(sketch, "E30.65.0", {"start": v(86.16, -31.54) * mm, "end": v(85.49, -31.93) * mm});
            skLineSegment(sketch, "E30.65.1", {"start": v(85.49, -31.93) * mm, "end": v(85.42, -31.2) * mm});
            skLineSegment(sketch, "E30.66.0", {"start": v(87.32, -32.03) * mm, "end": v(86.66, -32.45) * mm});
            skLineSegment(sketch, "E30.66.1", {"start": v(86.66, -32.45) * mm, "end": v(86.57, -31.72) * mm});
            skLineSegment(sketch, "E30.67.0", {"start": v(88.5, -32.47) * mm, "end": v(87.86, -32.91) * mm});
            skLineSegment(sketch, "E30.67.1", {"start": v(87.86, -32.91) * mm, "end": v(87.73, -32.2) * mm});
            skLineSegment(sketch, "E30.68.0", {"start": v(89.7, -32.86) * mm, "end": v(89.07, -33.33) * mm});
            skLineSegment(sketch, "E30.68.1", {"start": v(89.07, -33.33) * mm, "end": v(88.92, -32.61) * mm});
            skLineSegment(sketch, "E30.69.0", {"start": v(90.9, -33.2) * mm, "end": v(90.3, -33.7) * mm});
            skLineSegment(sketch, "E30.69.1", {"start": v(90.3, -33.7) * mm, "end": v(90.12, -32.98) * mm});
            skLineSegment(sketch, "E30.70.0", {"start": v(92.12, -33.48) * mm, "end": v(91.55, -34) * mm});
            skLineSegment(sketch, "E30.70.1", {"start": v(91.55, -34) * mm, "end": v(91.33, -33.3) * mm});
            skLineSegment(sketch, "E30.71.0", {"start": v(93.36, -33.72) * mm, "end": v(92.8, -34.26) * mm});
            skLineSegment(sketch, "E30.71.1", {"start": v(92.8, -34.26) * mm, "end": v(92.56, -33.57) * mm});
            skLineSegment(sketch, "E30.72.0", {"start": v(94.6, -33.9) * mm, "end": v(94.07, -34.47) * mm});
            skLineSegment(sketch, "E30.72.1", {"start": v(94.07, -34.47) * mm, "end": v(93.8, -33.79) * mm});
            skLineSegment(sketch, "E30.73.0", {"start": v(95.85, -34.03) * mm, "end": v(95.35, -34.62) * mm});
            skLineSegment(sketch, "E30.73.1", {"start": v(95.35, -34.62) * mm, "end": v(95.05, -33.95) * mm});
            skLineSegment(sketch, "E30.74.0", {"start": v(97.1, -34.11) * mm, "end": v(96.63, -34.72) * mm});
            skLineSegment(sketch, "E30.74.1", {"start": v(96.63, -34.72) * mm, "end": v(96.3, -34.07) * mm});
            skLineSegment(sketch, "E30.75.0", {"start": v(98.36, -34.14) * mm, "end": v(97.9, -34.77) * mm});
            skLineSegment(sketch, "E30.75.1", {"start": v(97.9, -34.77) * mm, "end": v(97.55, -34.13) * mm});
            skLineSegment(sketch, "E30.76.0", {"start": v(99.62, -34.11) * mm, "end": v(99.2, -34.76) * mm});
            skLineSegment(sketch, "E30.76.1", {"start": v(99.2, -34.76) * mm, "end": v(98.8, -34.13) * mm});
            skLineSegment(sketch, "E30.77.0", {"start": v(100.87, -34.03) * mm, "end": v(100.47, -34.7) * mm});
            skLineSegment(sketch, "E30.77.1", {"start": v(100.47, -34.7) * mm, "end": v(100.06, -34.09) * mm});
            skLineSegment(sketch, "E30.78.0", {"start": v(102.12, -33.9) * mm, "end": v(101.75, -34.58) * mm});
            skLineSegment(sketch, "E30.78.1", {"start": v(101.75, -34.58) * mm, "end": v(101.32, -34) * mm});
            skLineSegment(sketch, "E30.79.0", {"start": v(103.37, -33.72) * mm, "end": v(103.02, -34.41) * mm});
            skLineSegment(sketch, "E30.79.1", {"start": v(103.02, -34.41) * mm, "end": v(102.56, -33.84) * mm});
            skLineSegment(sketch, "E30.80.0", {"start": v(104.6, -33.48) * mm, "end": v(104.29, -34.2) * mm});
            skLineSegment(sketch, "E30.80.1", {"start": v(104.29, -34.2) * mm, "end": v(103.8, -33.64) * mm});
            skLineSegment(sketch, "E30.81.0", {"start": v(105.82, -33.2) * mm, "end": v(105.54, -33.92) * mm});
            skLineSegment(sketch, "E30.81.1", {"start": v(105.54, -33.92) * mm, "end": v(105.04, -33.39) * mm});
            skLineSegment(sketch, "E30.82.0", {"start": v(107.03, -32.86) * mm, "end": v(106.78, -33.6) * mm});
            skLineSegment(sketch, "E30.82.1", {"start": v(106.78, -33.6) * mm, "end": v(106.25, -33.08) * mm});
            skLineSegment(sketch, "E30.83.0", {"start": v(108.23, -32.47) * mm, "end": v(108, -33.21) * mm});
            skLineSegment(sketch, "E30.83.1", {"start": v(108, -33.21) * mm, "end": v(107.46, -32.72) * mm});
            skLineSegment(sketch, "E30.84.0", {"start": v(109.4, -32.03) * mm, "end": v(109.21, -32.78) * mm});
            skLineSegment(sketch, "E30.84.1", {"start": v(109.21, -32.78) * mm, "end": v(108.65, -32.32) * mm});
            skLineSegment(sketch, "E30.85.0", {"start": v(110.56, -31.54) * mm, "end": v(110.4, -32.3) * mm});
            skLineSegment(sketch, "E30.85.1", {"start": v(110.4, -32.3) * mm, "end": v(109.82, -31.86) * mm});
            skLineSegment(sketch, "E30.86.0", {"start": v(111.7, -31) * mm, "end": v(111.57, -31.77) * mm});
            skLineSegment(sketch, "E30.86.1", {"start": v(111.57, -31.77) * mm, "end": v(110.97, -31.36) * mm});
            skLineSegment(sketch, "E30.87.0", {"start": v(112.81, -30.43) * mm, "end": v(112.72, -31.2) * mm});
            skLineSegment(sketch, "E30.87.1", {"start": v(112.72, -31.2) * mm, "end": v(112.1, -30.8) * mm});
            skLineSegment(sketch, "E30.88.0", {"start": v(113.9, -29.8) * mm, "end": v(113.84, -30.57) * mm});
            skLineSegment(sketch, "E30.88.1", {"start": v(113.84, -30.57) * mm, "end": v(113.2, -30.2) * mm});
            skLineSegment(sketch, "E30.89.0", {"start": v(114.96, -29.12) * mm, "end": v(114.93, -29.9) * mm});
            skLineSegment(sketch, "E30.89.1", {"start": v(114.93, -29.9) * mm, "end": v(114.28, -29.56) * mm});
            skLineSegment(sketch, "E30.90.0", {"start": v(116, -28.4) * mm, "end": v(116, -29.18) * mm});
            skLineSegment(sketch, "E30.90.1", {"start": v(116, -29.18) * mm, "end": v(115.33, -28.88) * mm});
            skLineSegment(sketch, "E30.91.0", {"start": v(117, -27.65) * mm, "end": v(117.03, -28.42) * mm});
            skLineSegment(sketch, "E30.91.1", {"start": v(117.03, -28.42) * mm, "end": v(116.35, -28.14) * mm});
            skLineSegment(sketch, "E30.92.0", {"start": v(117.96, -26.85) * mm, "end": v(118.03, -27.62) * mm});
            skLineSegment(sketch, "E30.92.1", {"start": v(118.03, -27.62) * mm, "end": v(117.34, -27.37) * mm});
            skLineSegment(sketch, "E30.93.0", {"start": v(118.9, -26) * mm, "end": v(119, -26.78) * mm});
            skLineSegment(sketch, "E30.93.1", {"start": v(119, -26.78) * mm, "end": v(118.3, -26.55) * mm});
            skLineSegment(sketch, "E30.94.0", {"start": v(119.8, -25.13) * mm, "end": v(119.93, -25.9) * mm});
            skLineSegment(sketch, "E30.94.1", {"start": v(119.93, -25.9) * mm, "end": v(119.22, -25.7) * mm});
            skLineSegment(sketch, "E30.95.0", {"start": v(120.66, -24.21) * mm, "end": v(120.82, -24.97) * mm});
            skLineSegment(sketch, "E30.95.1", {"start": v(120.82, -24.97) * mm, "end": v(120.1, -24.8) * mm});
            skLineSegment(sketch, "E30.96.0", {"start": v(121.48, -23.26) * mm, "end": v(121.67, -24.01) * mm});
            skLineSegment(sketch, "E30.96.1", {"start": v(121.67, -24.01) * mm, "end": v(120.95, -23.88) * mm});
            skLineSegment(sketch, "E30.97.0", {"start": v(122.26, -22.28) * mm, "end": v(122.48, -23.02) * mm});
            skLineSegment(sketch, "E30.97.1", {"start": v(122.48, -23.02) * mm, "end": v(121.76, -22.91) * mm});
            skLineSegment(sketch, "E30.98.0", {"start": v(123, -21.26) * mm, "end": v(123.25, -22) * mm});
            skLineSegment(sketch, "E30.98.1", {"start": v(123.25, -22) * mm, "end": v(122.53, -21.92) * mm});
            skLineSegment(sketch, "E30.99.0", {"start": v(123.7, -20.21) * mm, "end": v(123.98, -20.93) * mm});
            skLineSegment(sketch, "E30.99.1", {"start": v(123.98, -20.93) * mm, "end": v(123.25, -20.9) * mm});
            skLineSegment(sketch, "E30.100.0", {"start": v(124.34, -19.14) * mm, "end": v(124.66, -19.85) * mm});
            skLineSegment(sketch, "E30.100.1", {"start": v(124.66, -19.85) * mm, "end": v(123.93, -19.83) * mm});
            skLineSegment(sketch, "E30.101.0", {"start": v(124.95, -18.04) * mm, "end": v(125.3, -18.73) * mm});
            skLineSegment(sketch, "E30.101.1", {"start": v(125.3, -18.73) * mm, "end": v(124.56, -18.75) * mm});
            skLineSegment(sketch, "E30.102.0", {"start": v(125.5, -16.91) * mm, "end": v(125.88, -17.6) * mm});
            skLineSegment(sketch, "E30.102.1", {"start": v(125.88, -17.6) * mm, "end": v(125.15, -17.64) * mm});
            skLineSegment(sketch, "E30.103.0", {"start": v(126.02, -15.76) * mm, "end": v(126.42, -16.43) * mm});
            skLineSegment(sketch, "E30.103.1", {"start": v(126.42, -16.43) * mm, "end": v(125.7, -16.5) * mm});
            skLineSegment(sketch, "E30.104.0", {"start": v(126.48, -14.6) * mm, "end": v(126.91, -15.24) * mm});
            skLineSegment(sketch, "E30.104.1", {"start": v(126.91, -15.24) * mm, "end": v(126.19, -15.35) * mm});
            skLineSegment(sketch, "E30.105.0", {"start": v(126.9, -13.4) * mm, "end": v(127.35, -14.03) * mm});
            skLineSegment(sketch, "E30.105.1", {"start": v(127.35, -14.03) * mm, "end": v(126.63, -14.18) * mm});
            skLineSegment(sketch, "E30.106.0", {"start": v(127.26, -12.2) * mm, "end": v(127.74, -12.81) * mm});
            skLineSegment(sketch, "E30.106.1", {"start": v(127.74, -12.81) * mm, "end": v(127.03, -12.98) * mm});
            skLineSegment(sketch, "E30.107.0", {"start": v(127.57, -10.99) * mm, "end": v(128.08, -11.57) * mm});
            skLineSegment(sketch, "E30.107.1", {"start": v(128.08, -11.57) * mm, "end": v(127.37, -11.77) * mm});
            skLineSegment(sketch, "E30.108.0", {"start": v(127.83, -9.76) * mm, "end": v(128.36, -10.32) * mm});
            skLineSegment(sketch, "E30.108.1", {"start": v(128.36, -10.32) * mm, "end": v(127.67, -10.55) * mm});
            skLineSegment(sketch, "E30.109.0", {"start": v(128.04, -8.52) * mm, "end": v(128.6, -9.06) * mm});
            skLineSegment(sketch, "E30.109.1", {"start": v(128.6, -9.06) * mm, "end": v(127.91, -9.32) * mm});
            skLineSegment(sketch, "E30.110.0", {"start": v(128.2, -7.27) * mm, "end": v(128.78, -7.8) * mm});
            skLineSegment(sketch, "E30.110.1", {"start": v(128.78, -7.8) * mm, "end": v(128.1, -8.08) * mm});
            skLineSegment(sketch, "E30.111.0", {"start": v(128.3, -6.02) * mm, "end": v(128.9, -6.51) * mm});
            skLineSegment(sketch, "E30.111.1", {"start": v(128.9, -6.51) * mm, "end": v(128.24, -6.83) * mm});
            skLineSegment(sketch, "E30.112.0", {"start": v(128.36, -4.77) * mm, "end": v(128.98, -5.23) * mm});
            skLineSegment(sketch, "E30.112.1", {"start": v(128.98, -5.23) * mm, "end": v(128.33, -5.58) * mm});
            skLineSegment(sketch, "E30.113.0", {"start": v(128.36, -3.5) * mm, "end": v(129, -3.95) * mm});
            skLineSegment(sketch, "E30.113.1", {"start": v(129, -3.95) * mm, "end": v(128.36, -4.32) * mm});
            skLineSegment(sketch, "E30.114.0", {"start": v(128.3, -2.25) * mm, "end": v(128.96, -2.67) * mm});
            skLineSegment(sketch, "E30.114.1", {"start": v(128.96, -2.67) * mm, "end": v(128.34, -3.06) * mm});
            skLineSegment(sketch, "E30.115.0", {"start": v(128.2, -1) * mm, "end": v(128.87, -1.39) * mm});
            skLineSegment(sketch, "E30.115.1", {"start": v(128.87, -1.39) * mm, "end": v(128.27, -1.8) * mm});
            skLineSegment(sketch, "E30.116.0", {"start": v(128.04, 0.25) * mm, "end": v(128.73, -0.11) * mm});
            skLineSegment(sketch, "E30.116.1", {"start": v(128.73, -0.11) * mm, "end": v(128.15, -0.56) * mm});
            skLineSegment(sketch, "E30.117.0", {"start": v(127.83, 1.48) * mm, "end": v(128.53, 1.16) * mm});
            skLineSegment(sketch, "E30.117.1", {"start": v(128.53, 1.16) * mm, "end": v(127.97, 0.69) * mm});
            skLineSegment(sketch, "E30.118.0", {"start": v(127.57, 2.71) * mm, "end": v(128.29, 2.41) * mm});
            skLineSegment(sketch, "E30.118.1", {"start": v(128.29, 2.41) * mm, "end": v(127.74, 1.92) * mm});
            skLineSegment(sketch, "E30.119.0", {"start": v(127.26, 3.93) * mm, "end": v(127.99, 3.66) * mm});
            skLineSegment(sketch, "E30.119.1", {"start": v(127.99, 3.66) * mm, "end": v(127.46, 3.15) * mm});
            skLineSegment(sketch, "E30.120.0", {"start": v(126.9, 5.13) * mm, "end": v(127.63, 4.9) * mm});
            skLineSegment(sketch, "E30.120.1", {"start": v(127.63, 4.9) * mm, "end": v(127.13, 4.36) * mm});
            skLineSegment(sketch, "E30.121.0", {"start": v(126.48, 6.32) * mm, "end": v(127.23, 6.11) * mm});
            skLineSegment(sketch, "E30.121.1", {"start": v(127.23, 6.11) * mm, "end": v(126.75, 5.56) * mm});
            skLineSegment(sketch, "E30.122.0", {"start": v(126.02, 7.49) * mm, "end": v(126.77, 7.31) * mm});
            skLineSegment(sketch, "E30.122.1", {"start": v(126.77, 7.31) * mm, "end": v(126.32, 6.74) * mm});
            skLineSegment(sketch, "E30.123.0", {"start": v(125.5, 8.64) * mm, "end": v(126.27, 8.5) * mm});
            skLineSegment(sketch, "E30.123.1", {"start": v(126.27, 8.5) * mm, "end": v(125.84, 7.9) * mm});
            skLineSegment(sketch, "E30.124.0", {"start": v(124.95, 9.76) * mm, "end": v(125.72, 9.65) * mm});
            skLineSegment(sketch, "E30.124.1", {"start": v(125.72, 9.65) * mm, "end": v(125.31, 9.04) * mm});
            skLineSegment(sketch, "E30.125.0", {"start": v(124.34, 10.86) * mm, "end": v(125.12, 10.78) * mm});
            skLineSegment(sketch, "E30.125.1", {"start": v(125.12, 10.78) * mm, "end": v(124.74, 10.16) * mm});
            skLineSegment(sketch, "E30.126.0", {"start": v(123.7, 11.94) * mm, "end": v(124.47, 11.9) * mm});
            skLineSegment(sketch, "E30.126.1", {"start": v(124.47, 11.9) * mm, "end": v(124.12, 11.25) * mm});
            skLineSegment(sketch, "E30.127.0", {"start": v(123, 12.98) * mm, "end": v(123.77, 12.97) * mm});
            skLineSegment(sketch, "E30.127.1", {"start": v(123.77, 12.97) * mm, "end": v(123.45, 12.31) * mm});
            skLineSegment(sketch, "E30.128.0", {"start": v(122.26, 14) * mm, "end": v(123.03, 14.02) * mm});
            skLineSegment(sketch, "E30.128.1", {"start": v(123.03, 14.02) * mm, "end": v(122.74, 13.35) * mm});
            skLineSegment(sketch, "E30.129.0", {"start": v(121.48, 14.99) * mm, "end": v(122.25, 15.04) * mm});
            skLineSegment(sketch, "E30.129.1", {"start": v(122.25, 15.04) * mm, "end": v(121.99, 14.35) * mm});
            skLineSegment(sketch, "E30.130.0", {"start": v(120.66, 15.94) * mm, "end": v(121.43, 16.02) * mm});
            skLineSegment(sketch, "E30.130.1", {"start": v(121.43, 16.02) * mm, "end": v(121.2, 15.33) * mm});
            skLineSegment(sketch, "E30.131.0", {"start": v(119.8, 16.85) * mm, "end": v(120.56, 16.97) * mm});
            skLineSegment(sketch, "E30.131.1", {"start": v(120.56, 16.97) * mm, "end": v(120.36, 16.27) * mm});
            skLineSegment(sketch, "E30.132.0", {"start": v(118.9, 17.73) * mm, "end": v(119.66, 17.88) * mm});
            skLineSegment(sketch, "E30.132.1", {"start": v(119.66, 17.88) * mm, "end": v(119.48, 17.17) * mm});
            skLineSegment(sketch, "E30.133.0", {"start": v(117.96, 18.57) * mm, "end": v(118.72, 18.75) * mm});
            skLineSegment(sketch, "E30.133.1", {"start": v(118.72, 18.75) * mm, "end": v(118.57, 18.03) * mm});
            skLineSegment(sketch, "E30.134.0", {"start": v(117, 19.37) * mm, "end": v(117.74, 19.58) * mm});
            skLineSegment(sketch, "E30.134.1", {"start": v(117.74, 19.58) * mm, "end": v(117.63, 18.86) * mm});
            skLineSegment(sketch, "E30.135.0", {"start": v(116, 20.13) * mm, "end": v(116.73, 20.37) * mm});
            skLineSegment(sketch, "E30.135.1", {"start": v(116.73, 20.37) * mm, "end": v(116.65, 19.65) * mm});
            skLineSegment(sketch, "E30.136.0", {"start": v(114.96, 20.85) * mm, "end": v(115.7, 21.12) * mm});
            skLineSegment(sketch, "E30.136.1", {"start": v(115.7, 21.12) * mm, "end": v(115.63, 20.4) * mm});
            skLineSegment(sketch, "E30.137.0", {"start": v(113.9, 21.52) * mm, "end": v(114.62, 21.83) * mm});
            skLineSegment(sketch, "E30.137.1", {"start": v(114.62, 21.83) * mm, "end": v(114.6, 21.1) * mm});
            skLineSegment(sketch, "E30.138.0", {"start": v(112.81, 22.15) * mm, "end": v(113.52, 22.48) * mm});
            skLineSegment(sketch, "E30.138.1", {"start": v(113.52, 22.48) * mm, "end": v(113.52, 21.75) * mm});
            skLineSegment(sketch, "E30.139.0", {"start": v(111.7, 22.73) * mm, "end": v(112.39, 23.1) * mm});
            skLineSegment(sketch, "E30.139.1", {"start": v(112.39, 23.1) * mm, "end": v(112.42, 22.36) * mm});
            skLineSegment(sketch, "E30.140.0", {"start": v(110.56, 23.27) * mm, "end": v(111.24, 23.66) * mm});
            skLineSegment(sketch, "E30.140.1", {"start": v(111.24, 23.66) * mm, "end": v(111.3, 22.93) * mm});
            skLineSegment(sketch, "E30.141.0", {"start": v(109.4, 23.76) * mm, "end": v(110.06, 24.17) * mm});
            skLineSegment(sketch, "E30.141.1", {"start": v(110.06, 24.17) * mm, "end": v(110.16, 23.45) * mm});
            skLineSegment(sketch, "E30.142.0", {"start": v(108.23, 24.2) * mm, "end": v(108.86, 24.64) * mm});
            skLineSegment(sketch, "E30.142.1", {"start": v(108.86, 24.64) * mm, "end": v(109, 23.92) * mm});
            skLineSegment(sketch, "E30.143.0", {"start": v(107.03, 24.58) * mm, "end": v(107.65, 25.05) * mm});
            skLineSegment(sketch, "E30.143.1", {"start": v(107.65, 25.05) * mm, "end": v(107.8, 24.34) * mm});
            skLineSegment(sketch, "E30.144.0", {"start": v(105.82, 24.92) * mm, "end": v(106.42, 25.42) * mm});
            skLineSegment(sketch, "E30.144.1", {"start": v(106.42, 25.42) * mm, "end": v(106.6, 24.7) * mm});
            skLineSegment(sketch, "E30.145.0", {"start": v(104.6, 25.2) * mm, "end": v(105.18, 25.73) * mm});
            skLineSegment(sketch, "E30.145.1", {"start": v(105.18, 25.73) * mm, "end": v(105.4, 25.03) * mm});
            skLineSegment(sketch, "E30.146.0", {"start": v(103.37, 25.44) * mm, "end": v(103.92, 25.99) * mm});
            skLineSegment(sketch, "E30.146.1", {"start": v(103.92, 25.99) * mm, "end": v(104.16, 25.3) * mm});
            skLineSegment(sketch, "E30.147.0", {"start": v(102.12, 25.63) * mm, "end": v(102.65, 26.2) * mm});
            skLineSegment(sketch, "E30.147.1", {"start": v(102.65, 26.2) * mm, "end": v(102.93, 25.51) * mm});
            skLineSegment(sketch, "E30.148.0", {"start": v(100.87, 25.76) * mm, "end": v(101.38, 26.35) * mm});
            skLineSegment(sketch, "E30.148.1", {"start": v(101.38, 26.35) * mm, "end": v(101.68, 25.68) * mm});
            skLineSegment(sketch, "E30.149.0", {"start": v(99.62, 25.84) * mm, "end": v(100.1, 26.45) * mm});
            skLineSegment(sketch, "E30.149.1", {"start": v(100.1, 26.45) * mm, "end": v(100.43, 25.8) * mm});
            skArc(sketch, "E31.trimOffspring", {"start": v(99.62, 25.84) * mm, "mid": v(99.4, 25.84) * mm, "end": v(99.17, 25.85) * mm});
            skArc(sketch, "E32.trimOffspring", {"start": v(100.87, 25.76) * mm, "mid": v(100.65, 25.78) * mm, "end": v(100.43, 25.8) * mm});
            skArc(sketch, "E33.trimOffspring", {"start": v(102.12, 25.63) * mm, "mid": v(101.9, 25.65) * mm, "end": v(101.68, 25.68) * mm});
            skArc(sketch, "E34.trimOffspring", {"start": v(103.37, 25.44) * mm, "mid": v(103.15, 25.48) * mm, "end": v(102.93, 25.51) * mm});
            skArc(sketch, "E35.trimOffspring", {"start": v(104.6, 25.2) * mm, "mid": v(104.38, 25.25) * mm, "end": v(104.16, 25.3) * mm});
            skArc(sketch, "E36.trimOffspring", {"start": v(105.82, 24.92) * mm, "mid": v(105.6, 24.97) * mm, "end": v(105.4, 25.03) * mm});
            skArc(sketch, "E37.trimOffspring", {"start": v(107.03, 24.58) * mm, "mid": v(106.82, 24.65) * mm, "end": v(106.6, 24.7) * mm});
            skArc(sketch, "E38.trimOffspring", {"start": v(108.23, 24.2) * mm, "mid": v(108.02, 24.27) * mm, "end": v(107.8, 24.34) * mm});
            skArc(sketch, "E39.trimOffspring", {"start": v(109.4, 23.76) * mm, "mid": v(109.2, 23.84) * mm, "end": v(109, 23.92) * mm});
            skArc(sketch, "E40.trimOffspring", {"start": v(110.56, 23.27) * mm, "mid": v(110.36, 23.36) * mm, "end": v(110.16, 23.45) * mm});
            skArc(sketch, "E41.trimOffspring", {"start": v(111.7, 22.73) * mm, "mid": v(111.5, 22.83) * mm, "end": v(111.3, 22.93) * mm});
            skArc(sketch, "E42.trimOffspring", {"start": v(112.81, 22.15) * mm, "mid": v(112.62, 22.26) * mm, "end": v(112.42, 22.36) * mm});
            skArc(sketch, "E43.trimOffspring", {"start": v(113.9, 21.52) * mm, "mid": v(113.71, 21.64) * mm, "end": v(113.52, 21.75) * mm});
            skArc(sketch, "E44.trimOffspring", {"start": v(114.96, 20.85) * mm, "mid": v(114.78, 20.97) * mm, "end": v(114.6, 21.1) * mm});
            skArc(sketch, "E45.trimOffspring", {"start": v(116, 20.13) * mm, "mid": v(115.82, 20.26) * mm, "end": v(115.63, 20.4) * mm});
            skArc(sketch, "E46.trimOffspring", {"start": v(117, 19.37) * mm, "mid": v(116.82, 19.51) * mm, "end": v(116.65, 19.65) * mm});
            skArc(sketch, "E47.trimOffspring", {"start": v(117.96, 18.57) * mm, "mid": v(117.8, 18.72) * mm, "end": v(117.63, 18.86) * mm});
            skArc(sketch, "E48.trimOffspring", {"start": v(118.9, 17.73) * mm, "mid": v(118.74, 17.88) * mm, "end": v(118.57, 18.03) * mm});
            skArc(sketch, "E49.trimOffspring", {"start": v(119.8, 16.85) * mm, "mid": v(119.64, 17.01) * mm, "end": v(119.48, 17.17) * mm});
            skArc(sketch, "E50.trimOffspring", {"start": v(120.66, 15.94) * mm, "mid": v(120.5, 16.1) * mm, "end": v(120.36, 16.27) * mm});
            skArc(sketch, "E51.trimOffspring", {"start": v(121.48, 14.99) * mm, "mid": v(121.33, 15.16) * mm, "end": v(121.2, 15.33) * mm});
            skArc(sketch, "E52.trimOffspring", {"start": v(122.26, 14) * mm, "mid": v(122.12, 14.18) * mm, "end": v(121.99, 14.35) * mm});
            skArc(sketch, "E53.trimOffspring", {"start": v(123, 12.98) * mm, "mid": v(122.87, 13.17) * mm, "end": v(122.74, 13.35) * mm});
            skArc(sketch, "E54.trimOffspring", {"start": v(123.7, 11.94) * mm, "mid": v(123.57, 12.13) * mm, "end": v(123.45, 12.31) * mm});
            skArc(sketch, "E55.trimOffspring", {"start": v(124.34, 10.86) * mm, "mid": v(124.23, 11.06) * mm, "end": v(124.12, 11.25) * mm});
            skArc(sketch, "E56.trimOffspring", {"start": v(124.95, 9.76) * mm, "mid": v(124.84, 9.96) * mm, "end": v(124.74, 10.16) * mm});
            skArc(sketch, "E57.trimOffspring", {"start": v(125.5, 8.64) * mm, "mid": v(125.41, 8.84) * mm, "end": v(125.31, 9.04) * mm});
            skArc(sketch, "E58.trimOffspring", {"start": v(126.02, 7.49) * mm, "mid": v(125.93, 7.7) * mm, "end": v(125.84, 7.9) * mm});
            skArc(sketch, "E59.trimOffspring", {"start": v(126.48, 6.32) * mm, "mid": v(126.4, 6.53) * mm, "end": v(126.32, 6.74) * mm});
            skArc(sketch, "E60.trimOffspring", {"start": v(126.9, 5.13) * mm, "mid": v(126.82, 5.34) * mm, "end": v(126.75, 5.56) * mm});
            skArc(sketch, "E61.trimOffspring", {"start": v(127.26, 3.93) * mm, "mid": v(127.2, 4.14) * mm, "end": v(127.13, 4.36) * mm});
            skArc(sketch, "E62.trimOffspring", {"start": v(127.57, 2.71) * mm, "mid": v(127.52, 2.93) * mm, "end": v(127.46, 3.15) * mm});
            skArc(sketch, "E63.trimOffspring", {"start": v(127.83, 1.48) * mm, "mid": v(127.79, 1.7) * mm, "end": v(127.74, 1.92) * mm});
            skArc(sketch, "E64.trimOffspring", {"start": v(128.04, 0.25) * mm, "mid": v(128, 0.47) * mm, "end": v(127.97, 0.69) * mm});
            skArc(sketch, "E65.trimOffspring", {"start": v(128.2, -1) * mm, "mid": v(128.17, -0.78) * mm, "end": v(128.15, -0.56) * mm});
            skArc(sketch, "E66.trimOffspring", {"start": v(128.3, -2.25) * mm, "mid": v(128.29, -2.03) * mm, "end": v(128.27, -1.8) * mm});
            skArc(sketch, "E67.trimOffspring", {"start": v(128.36, -3.5) * mm, "mid": v(128.35, -3.29) * mm, "end": v(128.34, -3.06) * mm});
            skArc(sketch, "E68.trimOffspring", {"start": v(128.36, -4.77) * mm, "mid": v(128.36, -4.54) * mm, "end": v(128.36, -4.32) * mm});
            skArc(sketch, "E69.trimOffspring", {"start": v(128.3, -6.02) * mm, "mid": v(128.32, -5.8) * mm, "end": v(128.33, -5.58) * mm});
            skArc(sketch, "E70.trimOffspring", {"start": v(128.2, -7.27) * mm, "mid": v(128.22, -7.05) * mm, "end": v(128.24, -6.83) * mm});
            skArc(sketch, "E71.trimOffspring", {"start": v(128.04, -8.52) * mm, "mid": v(128.07, -8.3) * mm, "end": v(128.1, -8.08) * mm});
            skArc(sketch, "E72.trimOffspring", {"start": v(127.83, -9.76) * mm, "mid": v(127.87, -9.54) * mm, "end": v(127.91, -9.32) * mm});
            skArc(sketch, "E73.trimOffspring", {"start": v(127.57, -10.99) * mm, "mid": v(127.62, -10.77) * mm, "end": v(127.67, -10.55) * mm});
            skArc(sketch, "E74.trimOffspring", {"start": v(127.26, -12.2) * mm, "mid": v(127.32, -11.99) * mm, "end": v(127.37, -11.77) * mm});
            skArc(sketch, "E75.trimOffspring", {"start": v(126.9, -13.4) * mm, "mid": v(126.96, -13.2) * mm, "end": v(127.03, -12.98) * mm});
            skArc(sketch, "E76.trimOffspring", {"start": v(126.48, -14.6) * mm, "mid": v(126.56, -14.39) * mm, "end": v(126.63, -14.18) * mm});
            skArc(sketch, "E77.trimOffspring", {"start": v(126.02, -15.76) * mm, "mid": v(126.1, -15.56) * mm, "end": v(126.19, -15.35) * mm});
            skArc(sketch, "E78.trimOffspring", {"start": v(125.5, -16.91) * mm, "mid": v(125.6, -16.7) * mm, "end": v(125.7, -16.5) * mm});
            skArc(sketch, "E79.trimOffspring", {"start": v(124.95, -18.04) * mm, "mid": v(125.05, -17.84) * mm, "end": v(125.15, -17.64) * mm});
            skArc(sketch, "E80.trimOffspring", {"start": v(124.34, -19.14) * mm, "mid": v(124.45, -18.94) * mm, "end": v(124.56, -18.75) * mm});
            skArc(sketch, "E81.trimOffspring", {"start": v(123.7, -20.21) * mm, "mid": v(123.81, -20.02) * mm, "end": v(123.93, -19.83) * mm});
            skArc(sketch, "E82.trimOffspring", {"start": v(123, -21.26) * mm, "mid": v(123.12, -21.08) * mm, "end": v(123.25, -20.9) * mm});
            skArc(sketch, "E83.trimOffspring", {"start": v(122.26, -22.28) * mm, "mid": v(122.4, -22.1) * mm, "end": v(122.53, -21.92) * mm});
            skArc(sketch, "E84.trimOffspring", {"start": v(121.48, -23.26) * mm, "mid": v(121.62, -23.09) * mm, "end": v(121.76, -22.91) * mm});
            skArc(sketch, "E85.trimOffspring", {"start": v(120.66, -24.21) * mm, "mid": v(120.8, -24.04) * mm, "end": v(120.95, -23.88) * mm});
            skArc(sketch, "E86.trimOffspring", {"start": v(119.8, -25.13) * mm, "mid": v(119.95, -24.97) * mm, "end": v(120.1, -24.8) * mm});
            skArc(sketch, "E87.trimOffspring", {"start": v(118.9, -26) * mm, "mid": v(119.06, -25.85) * mm, "end": v(119.22, -25.7) * mm});
            skArc(sketch, "E88.trimOffspring", {"start": v(117.96, -26.85) * mm, "mid": v(118.13, -26.7) * mm, "end": v(118.3, -26.55) * mm});
            skArc(sketch, "E89.trimOffspring", {"start": v(117, -27.65) * mm, "mid": v(117.17, -27.5) * mm, "end": v(117.34, -27.37) * mm});
            skArc(sketch, "E90.trimOffspring", {"start": v(116, -28.4) * mm, "mid": v(116.18, -28.28) * mm, "end": v(116.35, -28.14) * mm});
            skArc(sketch, "E91.trimOffspring", {"start": v(114.96, -29.12) * mm, "mid": v(115.15, -29) * mm, "end": v(115.33, -28.88) * mm});
            skArc(sketch, "E92.trimOffspring", {"start": v(113.9, -29.8) * mm, "mid": v(114.1, -29.68) * mm, "end": v(114.28, -29.56) * mm});
            skArc(sketch, "E93.trimOffspring", {"start": v(112.81, -30.43) * mm, "mid": v(113, -30.32) * mm, "end": v(113.2, -30.2) * mm});
            skArc(sketch, "E94.trimOffspring", {"start": v(111.7, -31) * mm, "mid": v(111.9, -30.9) * mm, "end": v(112.1, -30.8) * mm});
            skArc(sketch, "E95.trimOffspring", {"start": v(110.56, -31.54) * mm, "mid": v(110.77, -31.45) * mm, "end": v(110.97, -31.36) * mm});
            skArc(sketch, "E96.trimOffspring", {"start": v(109.4, -32.03) * mm, "mid": v(109.61, -31.95) * mm, "end": v(109.82, -31.86) * mm});
            skArc(sketch, "E97.trimOffspring", {"start": v(108.23, -32.47) * mm, "mid": v(108.44, -32.4) * mm, "end": v(108.65, -32.32) * mm});
            skArc(sketch, "E98.trimOffspring", {"start": v(107.03, -32.86) * mm, "mid": v(107.25, -32.8) * mm, "end": v(107.46, -32.72) * mm});
            skArc(sketch, "E99.trimOffspring", {"start": v(105.82, -33.2) * mm, "mid": v(106.04, -33.14) * mm, "end": v(106.25, -33.08) * mm});
            skArc(sketch, "E100.trimOffspring", {"start": v(104.6, -33.48) * mm, "mid": v(104.82, -33.43) * mm, "end": v(105.04, -33.39) * mm});
            skArc(sketch, "E101.trimOffspring", {"start": v(103.37, -33.72) * mm, "mid": v(103.59, -33.68) * mm, "end": v(103.8, -33.64) * mm});
            skArc(sketch, "E102.trimOffspring", {"start": v(102.12, -33.9) * mm, "mid": v(102.34, -33.87) * mm, "end": v(102.56, -33.84) * mm});
            skArc(sketch, "E103.trimOffspring", {"start": v(100.87, -34.03) * mm, "mid": v(101.1, -34.01) * mm, "end": v(101.32, -34) * mm});
            skArc(sketch, "E104.trimOffspring", {"start": v(99.62, -34.11) * mm, "mid": v(99.84, -34.1) * mm, "end": v(100.06, -34.09) * mm});
            skArc(sketch, "E105.trimOffspring", {"start": v(98.36, -34.14) * mm, "mid": v(98.59, -34.14) * mm, "end": v(98.8, -34.13) * mm});
            skArc(sketch, "E106.trimOffspring", {"start": v(97.1, -34.11) * mm, "mid": v(97.33, -34.12) * mm, "end": v(97.55, -34.13) * mm});
            skArc(sketch, "E107.trimOffspring", {"start": v(95.85, -34.03) * mm, "mid": v(96.07, -34.05) * mm, "end": v(96.3, -34.07) * mm});
            skArc(sketch, "E108.trimOffspring", {"start": v(94.6, -33.9) * mm, "mid": v(94.82, -33.93) * mm, "end": v(95.05, -33.95) * mm});
            skArc(sketch, "E109.trimOffspring", {"start": v(93.36, -33.72) * mm, "mid": v(93.58, -33.75) * mm, "end": v(93.8, -33.79) * mm});
            skArc(sketch, "E110.trimOffspring", {"start": v(92.12, -33.48) * mm, "mid": v(92.34, -33.53) * mm, "end": v(92.56, -33.57) * mm});
            skArc(sketch, "E111.trimOffspring", {"start": v(90.9, -33.2) * mm, "mid": v(91.12, -33.25) * mm, "end": v(91.33, -33.3) * mm});
            skArc(sketch, "E112.trimOffspring", {"start": v(89.7, -32.86) * mm, "mid": v(89.9, -32.92) * mm, "end": v(90.12, -32.98) * mm});
            skArc(sketch, "E113.trimOffspring", {"start": v(88.5, -32.47) * mm, "mid": v(88.7, -32.54) * mm, "end": v(88.92, -32.61) * mm});
            skArc(sketch, "E114.trimOffspring", {"start": v(87.32, -32.03) * mm, "mid": v(87.53, -32.11) * mm, "end": v(87.73, -32.2) * mm});
            skArc(sketch, "E115.trimOffspring", {"start": v(86.16, -31.54) * mm, "mid": v(86.36, -31.63) * mm, "end": v(86.57, -31.72) * mm});
            skArc(sketch, "E116.trimOffspring", {"start": v(85.02, -31) * mm, "mid": v(85.22, -31.1) * mm, "end": v(85.42, -31.2) * mm});
            skArc(sketch, "E117.trimOffspring", {"start": v(83.9, -30.43) * mm, "mid": v(84.1, -30.53) * mm, "end": v(84.3, -30.64) * mm});
            skArc(sketch, "E118.trimOffspring", {"start": v(82.82, -29.8) * mm, "mid": v(83.01, -29.91) * mm, "end": v(83.2, -30.03) * mm});
            skArc(sketch, "E119.trimOffspring", {"start": v(81.76, -29.12) * mm, "mid": v(81.95, -29.25) * mm, "end": v(82.13, -29.37) * mm});
            skArc(sketch, "E120.trimOffspring", {"start": v(80.73, -28.4) * mm, "mid": v(80.9, -28.54) * mm, "end": v(81.1, -28.67) * mm});
            skArc(sketch, "E121.trimOffspring", {"start": v(79.73, -27.65) * mm, "mid": v(79.9, -27.79) * mm, "end": v(80.08, -27.92) * mm});
            skArc(sketch, "E122.trimOffspring", {"start": v(78.76, -26.85) * mm, "mid": v(78.93, -27) * mm, "end": v(79.1, -27.14) * mm});
            skArc(sketch, "E123.trimOffspring", {"start": v(77.83, -26) * mm, "mid": v(77.99, -26.16) * mm, "end": v(78.15, -26.3) * mm});
            skArc(sketch, "E124.trimOffspring", {"start": v(76.93, -25.13) * mm, "mid": v(77.08, -25.29) * mm, "end": v(77.24, -25.44) * mm});
            skArc(sketch, "E125.trimOffspring", {"start": v(76.07, -24.21) * mm, "mid": v(76.22, -24.38) * mm, "end": v(76.37, -24.54) * mm});
            skArc(sketch, "E126.trimOffspring", {"start": v(75.25, -23.26) * mm, "mid": v(75.39, -23.43) * mm, "end": v(75.53, -23.6) * mm});
            skArc(sketch, "E127.trimOffspring", {"start": v(74.47, -22.28) * mm, "mid": v(74.6, -22.45) * mm, "end": v(74.74, -22.63) * mm});
            skArc(sketch, "E128.trimOffspring", {"start": v(73.73, -21.26) * mm, "mid": v(73.86, -21.44) * mm, "end": v(73.99, -21.62) * mm});
            skArc(sketch, "E129.trimOffspring", {"start": v(73.03, -20.21) * mm, "mid": v(73.15, -20.4) * mm, "end": v(73.27, -20.59) * mm});
            skArc(sketch, "E130.trimOffspring", {"start": v(72.38, -19.14) * mm, "mid": v(72.5, -19.33) * mm, "end": v(72.6, -19.52) * mm});
            skArc(sketch, "E131.trimOffspring", {"start": v(71.78, -18.04) * mm, "mid": v(71.88, -18.23) * mm, "end": v(71.99, -18.43) * mm});
            skArc(sketch, "E132.trimOffspring", {"start": v(71.22, -16.91) * mm, "mid": v(71.31, -17.11) * mm, "end": v(71.41, -17.31) * mm});
            skArc(sketch, "E133.trimOffspring", {"start": v(70.7, -15.76) * mm, "mid": v(70.8, -15.97) * mm, "end": v(70.88, -16.17) * mm});
            skArc(sketch, "E134.trimOffspring", {"start": v(70.24, -14.6) * mm, "mid": v(70.32, -14.8) * mm, "end": v(70.4, -15.01) * mm});
            skArc(sketch, "E135.trimOffspring", {"start": v(69.83, -13.4) * mm, "mid": v(69.9, -13.62) * mm, "end": v(69.97, -13.83) * mm});
            skArc(sketch, "E136.trimOffspring", {"start": v(69.47, -12.2) * mm, "mid": v(69.53, -12.42) * mm, "end": v(69.6, -12.63) * mm});
            skArc(sketch, "E137.trimOffspring", {"start": v(69.15, -10.99) * mm, "mid": v(69.2, -11.2) * mm, "end": v(69.26, -11.42) * mm});
            skArc(sketch, "E138.trimOffspring", {"start": v(68.9, -9.76) * mm, "mid": v(68.94, -9.98) * mm, "end": v(68.98, -10.2) * mm});
            skArc(sketch, "E139.trimOffspring", {"start": v(68.68, -8.52) * mm, "mid": v(68.72, -8.74) * mm, "end": v(68.75, -8.96) * mm});
            skArc(sketch, "E140.trimOffspring", {"start": v(68.53, -7.27) * mm, "mid": v(68.55, -7.5) * mm, "end": v(68.58, -7.72) * mm});
            skArc(sketch, "E141.trimOffspring", {"start": v(68.42, -6.02) * mm, "mid": v(68.44, -6.24) * mm, "end": v(68.45, -6.47) * mm});
            skArc(sketch, "E142.trimOffspring", {"start": v(68.37, -4.77) * mm, "mid": v(68.37, -4.99) * mm, "end": v(68.38, -5.21) * mm});
            skArc(sketch, "E143.trimOffspring", {"start": v(68.37, -3.5) * mm, "mid": v(68.37, -3.73) * mm, "end": v(68.36, -3.96) * mm});
            skArc(sketch, "E144.trimOffspring", {"start": v(68.42, -2.25) * mm, "mid": v(68.4, -2.48) * mm, "end": v(68.4, -2.7) * mm});
            skArc(sketch, "E145.trimOffspring", {"start": v(68.53, -1) * mm, "mid": v(68.5, -1.22) * mm, "end": v(68.48, -1.45) * mm});
            skArc(sketch, "E146.trimOffspring", {"start": v(68.68, 0.25) * mm, "mid": v(68.65, 0.02) * mm, "end": v(68.62, -0.2) * mm});
            skArc(sketch, "E147.trimOffspring", {"start": v(68.9, 1.48) * mm, "mid": v(68.85, 1.26) * mm, "end": v(68.81, 1.05) * mm});
            skArc(sketch, "E148.trimOffspring", {"start": v(69.15, 2.71) * mm, "mid": v(69.1, 2.5) * mm, "end": v(69.06, 2.28) * mm});
            skArc(sketch, "E149.trimOffspring", {"start": v(69.47, 3.93) * mm, "mid": v(69.4, 3.72) * mm, "end": v(69.35, 3.5) * mm});
            skArc(sketch, "E150.trimOffspring", {"start": v(69.83, 5.13) * mm, "mid": v(69.76, 4.92) * mm, "end": v(69.7, 4.7) * mm});
            skArc(sketch, "E151.trimOffspring", {"start": v(70.24, 6.32) * mm, "mid": v(70.17, 6.11) * mm, "end": v(70.1, 5.9) * mm});
            skArc(sketch, "E152.trimOffspring", {"start": v(70.7, 7.49) * mm, "mid": v(70.62, 7.28) * mm, "end": v(70.54, 7.08) * mm});
            skArc(sketch, "E153.trimOffspring", {"start": v(71.22, 8.64) * mm, "mid": v(71.12, 8.43) * mm, "end": v(71.03, 8.23) * mm});
            skArc(sketch, "E154.trimOffspring", {"start": v(71.78, 9.76) * mm, "mid": v(71.67, 9.56) * mm, "end": v(71.57, 9.36) * mm});
            skArc(sketch, "E155.trimOffspring", {"start": v(72.38, 10.86) * mm, "mid": v(72.27, 10.67) * mm, "end": v(72.16, 10.47) * mm});
            skArc(sketch, "E156.trimOffspring", {"start": v(73.03, 11.94) * mm, "mid": v(72.91, 11.75) * mm, "end": v(72.8, 11.56) * mm});
            skArc(sketch, "E157.trimOffspring", {"start": v(73.73, 12.98) * mm, "mid": v(73.6, 12.8) * mm, "end": v(73.48, 12.62) * mm});
            skArc(sketch, "E158.trimOffspring", {"start": v(74.47, 14) * mm, "mid": v(74.33, 13.82) * mm, "end": v(74.2, 13.64) * mm});
            skArc(sketch, "E159.trimOffspring", {"start": v(75.25, 14.99) * mm, "mid": v(75.1, 14.81) * mm, "end": v(74.97, 14.64) * mm});
            skArc(sketch, "E160.trimOffspring", {"start": v(76.07, 15.94) * mm, "mid": v(75.92, 15.77) * mm, "end": v(75.77, 15.6) * mm});
            skArc(sketch, "E161.trimOffspring", {"start": v(76.93, 16.85) * mm, "mid": v(76.77, 16.7) * mm, "end": v(76.62, 16.53) * mm});
            skArc(sketch, "E162.trimOffspring", {"start": v(77.83, 17.73) * mm, "mid": v(77.66, 17.58) * mm, "end": v(77.5, 17.42) * mm});
            skArc(sketch, "E163.trimOffspring", {"start": v(78.76, 18.57) * mm, "mid": v(78.6, 18.43) * mm, "end": v(78.42, 18.28) * mm});
            skArc(sketch, "E164.trimOffspring", {"start": v(79.73, 19.37) * mm, "mid": v(79.55, 19.23) * mm, "end": v(79.38, 19.1) * mm});
            skArc(sketch, "E165.trimOffspring", {"start": v(80.73, 20.13) * mm, "mid": v(80.55, 20) * mm, "end": v(80.37, 19.87) * mm});
            skArc(sketch, "E166.trimOffspring", {"start": v(81.76, 20.85) * mm, "mid": v(81.58, 20.73) * mm, "end": v(81.4, 20.6) * mm});
            skArc(sketch, "E167.trimOffspring", {"start": v(82.82, 21.52) * mm, "mid": v(82.63, 21.4) * mm, "end": v(82.44, 21.29) * mm});
            skArc(sketch, "E168.trimOffspring", {"start": v(83.9, 22.15) * mm, "mid": v(83.71, 22.04) * mm, "end": v(83.52, 21.93) * mm});
            skArc(sketch, "E169.trimOffspring", {"start": v(85.02, 22.73) * mm, "mid": v(84.82, 22.63) * mm, "end": v(84.63, 22.53) * mm});
            skArc(sketch, "E170.trimOffspring", {"start": v(86.16, 23.27) * mm, "mid": v(85.96, 23.18) * mm, "end": v(85.75, 23.08) * mm});
            skArc(sketch, "E171.trimOffspring", {"start": v(87.32, 23.76) * mm, "mid": v(87.11, 23.67) * mm, "end": v(86.9, 23.59) * mm});
            skArc(sketch, "E172.trimOffspring", {"start": v(88.5, 24.2) * mm, "mid": v(88.29, 24.12) * mm, "end": v(88.08, 24.04) * mm});
            skArc(sketch, "E173.trimOffspring", {"start": v(89.7, 24.58) * mm, "mid": v(89.48, 24.52) * mm, "end": v(89.27, 24.45) * mm});
            skArc(sketch, "E174.trimOffspring", {"start": v(90.9, 24.92) * mm, "mid": v(90.69, 24.86) * mm, "end": v(90.47, 24.8) * mm});
            skArc(sketch, "E175.trimOffspring", {"start": v(92.12, 25.2) * mm, "mid": v(91.9, 25.16) * mm, "end": v(91.69, 25.11) * mm});
            skArc(sketch, "E176.trimOffspring", {"start": v(93.36, 25.44) * mm, "mid": v(93.14, 25.4) * mm, "end": v(92.92, 25.36) * mm});
            skArc(sketch, "E177.trimOffspring", {"start": v(94.6, 25.63) * mm, "mid": v(94.38, 25.6) * mm, "end": v(94.16, 25.57) * mm});
            skArc(sketch, "E178.trimOffspring", {"start": v(95.85, 25.76) * mm, "mid": v(95.63, 25.74) * mm, "end": v(95.4, 25.72) * mm});
            skArc(sketch, "E179.trimOffspring", {"start": v(97.1, 25.84) * mm, "mid": v(96.88, 25.83) * mm, "end": v(96.66, 25.81) * mm});
            skCircle(sketch, "E180.1.6.0", {"center": v(114.2, 8.49) * mm, "radius": 7.25 * mm});
            skLineSegment(sketch, "E180.2.6.0", {"start": v(98.36, -4.14) * mm, "end": v(119.86, 13) * mm, "construction": true});
            skSolve(sketch);
        }
        {
            var Q0;
            Q0=makeQuery(id+"F19.imprint","IMPRINT",FACE,{"disambiguationData":[TD([[makeQuery(id+"F19.imprint","IMPRINT",EDGE,{"derivedFrom":sQuery(id+"F19.wireOp",EDGE,"E19")}),1.0]])]});
            extrude(context, id + "F20", {"entities" : qUnion([Q0]), "depth" : 17 * mm});
        }
        {
            var Q0;
            Q0=makeQuery(id+"F19.imprint","IMPRINT",FACE,{"disambiguationData":[TD([[makeQuery(id+"F19.imprint","IMPRINT",EDGE,{"derivedFrom":sQuery(id+"F19.wireOp",EDGE,"E21")}),-1.0]])]});
            extrude(context, id + "F21", {"entities" : qUnion([Q0]), "depth" : 7 * mm});
        }
        {
            var Q0;
            {var subQ0=sQuery(id+"F19.wireOp",EDGE,"E25");var subQ1=sQuery(id+"F19.wireOp",EDGE,"E20");var subQ2=makeQuery(id+"F19.imprint","INTERSECT",VERTEX,{"derivedFrom":[subQ1,subQ0]});Q0=makeQuery(id+"F19.imprint","IMPRINT",FACE,{"disambiguationData":[TD([[makeQuery(id+"F19.imprint","IMPRINT",EDGE,{"disambiguationData":[TD([[subQ2,-1.0]])],"derivedFrom":subQ1}),1.0]])]});}
            var Q1;
            {var subQ0=sQuery(id+"F19.wireOp",EDGE,"E26.1.0");var subQ1=sQuery(id+"F19.wireOp",EDGE,"E20");var subQ2=makeQuery(id+"F19.imprint","INTERSECT",VERTEX,{"derivedFrom":[subQ1,subQ0]});Q1=makeQuery(id+"F19.imprint","IMPRINT",FACE,{"disambiguationData":[TD([[makeQuery(id+"F19.imprint","IMPRINT",EDGE,{"disambiguationData":[TD([[subQ2,-1.0]])],"derivedFrom":subQ1}),1.0]])]});}
            var Q2;
            {var subQ0=sQuery(id+"F19.wireOp",EDGE,"E26.2.0");var subQ1=sQuery(id+"F19.wireOp",EDGE,"E20");var subQ2=makeQuery(id+"F19.imprint","INTERSECT",VERTEX,{"derivedFrom":[subQ1,subQ0]});Q2=makeQuery(id+"F19.imprint","IMPRINT",FACE,{"disambiguationData":[TD([[makeQuery(id+"F19.imprint","IMPRINT",EDGE,{"disambiguationData":[TD([[subQ2,-1.0]])],"derivedFrom":subQ1}),1.0]])]});}
            var Q3;
            {var subQ0=sQuery(id+"F19.wireOp",EDGE,"E26.3.0");var subQ1=sQuery(id+"F19.wireOp",EDGE,"E20");var subQ2=makeQuery(id+"F19.imprint","INTERSECT",VERTEX,{"derivedFrom":[subQ1,subQ0]});Q3=makeQuery(id+"F19.imprint","IMPRINT",FACE,{"disambiguationData":[TD([[makeQuery(id+"F19.imprint","IMPRINT",EDGE,{"disambiguationData":[TD([[subQ2,-1.0]])],"derivedFrom":subQ1}),1.0]])]});}
            var Q4;
            {var subQ0=sQuery(id+"F19.wireOp",EDGE,"E26.5.0");var subQ1=sQuery(id+"F19.wireOp",EDGE,"E20");var subQ2=makeQuery(id+"F19.imprint","INTERSECT",VERTEX,{"derivedFrom":[subQ1,subQ0]});Q4=makeQuery(id+"F19.imprint","IMPRINT",FACE,{"disambiguationData":[TD([[makeQuery(id+"F19.imprint","IMPRINT",EDGE,{"disambiguationData":[TD([[subQ2,1.0]])],"derivedFrom":subQ1}),1.0]])]});}
            var Q5;
            {var subQ0=sQuery(id+"F19.wireOp",EDGE,"E25");var subQ1=sQuery(id+"F19.wireOp",EDGE,"E20");var subQ2=makeQuery(id+"F19.imprint","INTERSECT",VERTEX,{"derivedFrom":[subQ1,subQ0]});Q5=makeQuery(id+"F19.imprint","IMPRINT",FACE,{"disambiguationData":[TD([[makeQuery(id+"F19.imprint","IMPRINT",EDGE,{"disambiguationData":[TD([[subQ2,1.0]])],"derivedFrom":subQ1}),1.0]])]});}
            var Q6;
            {var subQ0=sQuery(id+"F19.wireOp",EDGE,"E180.1.6.0");var subQ1=sQuery(id+"F19.wireOp",EDGE,"E20");var subQ2=makeQuery(id+"F19.imprint","INTERSECT",VERTEX,{"derivedFrom":[subQ1,subQ0]});Q6=makeQuery(id+"F19.imprint","IMPRINT",FACE,{"disambiguationData":[TD([[makeQuery(id+"F19.imprint","IMPRINT",EDGE,{"disambiguationData":[TD([[subQ2,1.0]])],"derivedFrom":subQ1}),1.0]])]});}
            extrude(context, id + "F22", {"entities" : qUnion([Q0, Q1, Q2, Q3, Q4, Q5, Q6]), "depth" : 3 * mm});
        }
        {
            var Q0;
            Q0=makeQuery(id+"F19.imprint","IMPRINT",FACE,{"disambiguationData":[TD([[makeQuery(id+"F19.imprint","IMPRINT",EDGE,{"derivedFrom":sQuery(id+"F19.wireOp",EDGE,"E21")}),1.0]])]});
            extrude(context, id + "F23", {"entities" : qUnion([Q0]), "operationType" : NewBodyOperationType.ADD, "depth" : 1 * mm});
        }
        {
            var Q0;
            Q0=makeQuery(id+"F3.opExtrude","CAP_EDGE",EDGE,{"disambiguationData":[OSD([sQuery(id+"F2.wireOp",EDGE,"E3.bottom")])],"isStart":false});
            var Q1;
            Q1=makeQuery(id+"F3.opExtrude","CAP_EDGE",EDGE,{"disambiguationData":[OSD([sQuery(id+"F2.wireOp",EDGE,"E3.top")])],"isStart":false});
            var Q2;
            Q2=makeQuery(id+"F3.opExtrude","CAP_EDGE",EDGE,{"disambiguationData":[OSD([sQuery(id+"F2.wireOp",EDGE,"E4.bottom")])],"isStart":false});
            var Q3;
            Q3=makeQuery(id+"F3.opExtrude","CAP_EDGE",EDGE,{"disambiguationData":[OSD([sQuery(id+"F2.wireOp",EDGE,"E4.top")])],"isStart":false});
            fillet(context, id + "F24", {"entities" : qUnion([Q0, Q1, Q2, Q3]), "radius" : 2 * mm, "tangentPropagation" : true, "allowEdgeOverflow" : false});
        }
        {
            var Q0;
            Q0=makeQuery(id+"F1.opExtrude","CAP_EDGE",EDGE,{"disambiguationData":[OSD([sQuery(id+"F0.wireOp",EDGE,"E2")])],"isStart":false});
            var Q1;
            Q1=makeQuery(id+"F1.opExtrude","CAP_EDGE",EDGE,{"disambiguationData":[OSD([sQuery(id+"F0.wireOp",EDGE,"E1")])],"isStart":false});
            var Q2;
            Q2=makeQuery(id+"FZJ4iVzhifTyHTz_1.1.F5.boolean.opBoolean","COPY",EDGE,{"derivedFrom":makeQuery(id+"FZJ4iVzhifTyHTz_1.1.F5.opExtrude","CAP_EDGE",EDGE,{"disambiguationData":[OSD([sQuery(id+"F4.wireOp",EDGE,"E5")])],"isStart":true})});
            var Q3;
            Q3=makeQuery(id+"F5.boolean.opBoolean","COPY",EDGE,{"derivedFrom":makeQuery(id+"F5.opExtrude","CAP_EDGE",EDGE,{"disambiguationData":[OSD([sQuery(id+"F4.wireOp",EDGE,"E5")])],"isStart":true})});
            fillet(context, id + "F25", {"entities" : qUnion([Q0, Q1, Q2, Q3]), "radius" : .5 * mm, "tangentPropagation" : true, "allowEdgeOverflow" : false});
        }
    });
